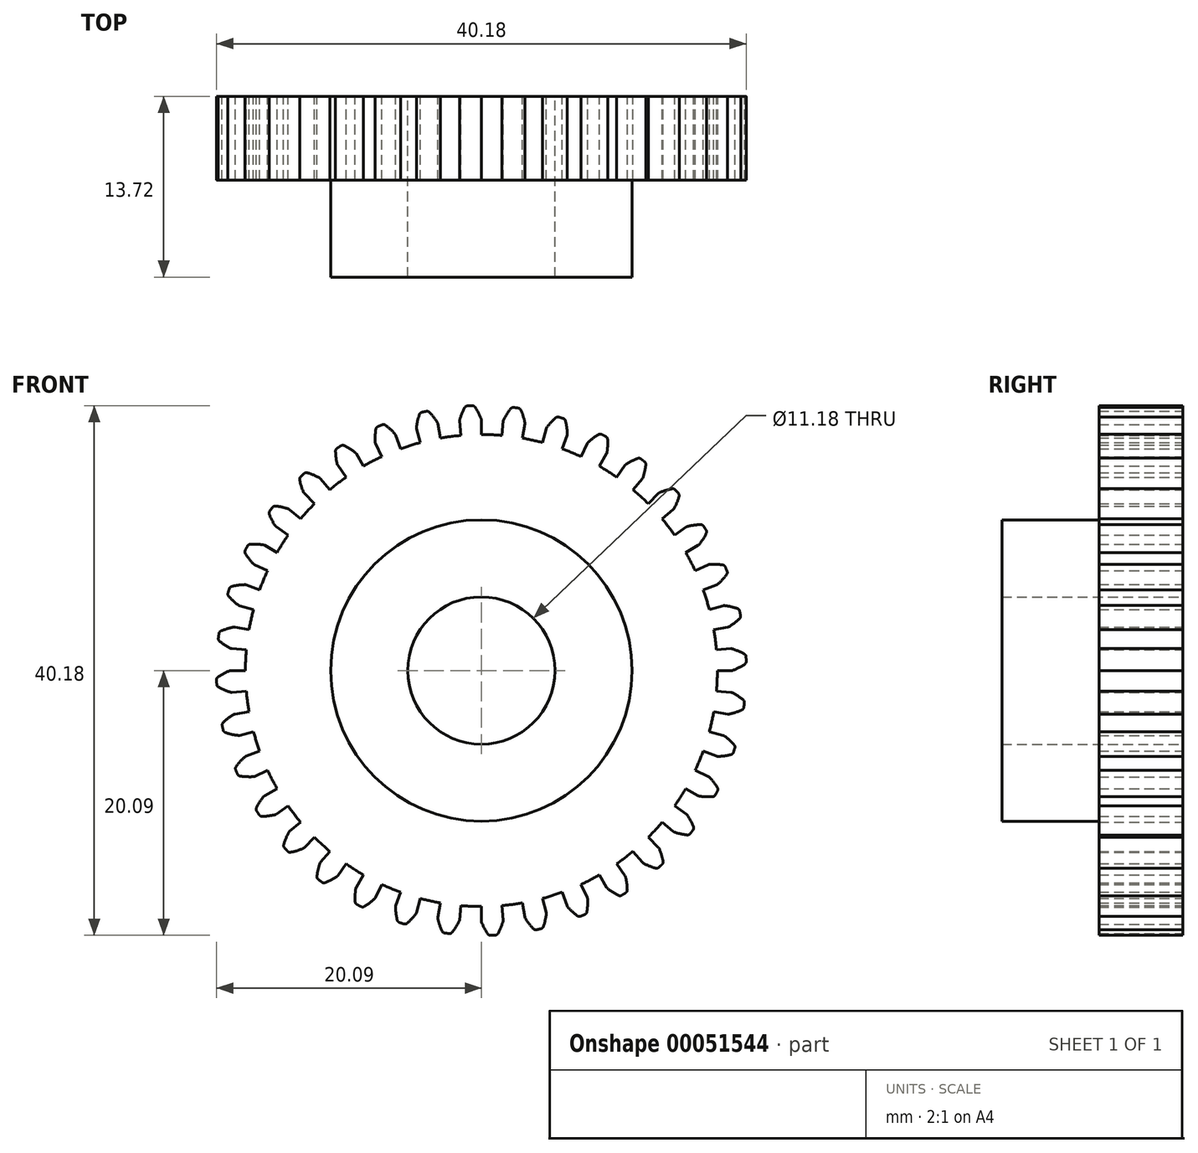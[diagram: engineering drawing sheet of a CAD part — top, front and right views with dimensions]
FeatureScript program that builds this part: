
annotation { "Feature Type Name" : "Feature", "Feature Type Description" : "" }
export const myFeature = defineFeature(function(context is Context, id is Id, definition is map)
    precondition{}
    {
        {
            var Q0;
            Q0=qCreatedBy(makeId("Front.planeOp"),FACE);
            var sketch = newSketch(context, id + "F0", { "sketchPlane" : qUnion([Q0])});
            skArc(sketch, "E0", {"start": v(-0.7, 20.1) * mm, "mid": v(-0.79, 20.09) * mm, "end": v(-0.88, 20.08) * mm});
            skCircle(sketch, "E1", {"center": v(0, 0) * mm, "radius": 17.9 * mm});
            skArc(sketch, "E2.trimOffspring", {"start": v(-0.02, 19.1) * mm, "mid": v(-0.23, 19.55) * mm, "end": v(-0.48, 19.98) * mm});
            skLineSegment(sketch, "E3", {"start": v(0, 19) * mm, "end": v(0, 17.9) * mm});
            skArc(sketch, "E4.MirrorCS", {"start": v(-1.05, 20.08) * mm, "mid": v(-0.97, 20.08) * mm, "end": v(-0.88, 20.08) * mm});
            skLineSegment(sketch, "E5.MirrorCS", {"start": v(-1.66, 18.93) * mm, "end": v(-1.56, 17.83) * mm});
            skArc(sketch, "E6.MirrorCS", {"start": v(-1.65, 19.02) * mm, "mid": v(-1.48, 19.5) * mm, "end": v(-1.26, 19.94) * mm});
            skPoint(sketch, "E7.visualSharp", {"position": v(-1.2, 20.07) * mm});
            skArc(sketch, "E7.filletArc", {"start": v(-1.05, 20.08) * mm, "mid": v(-1.18, 20.04) * mm, "end": v(-1.26, 19.94) * mm});
            skPoint(sketch, "E8.visualSharp", {"position": v(-0.56, 20.1) * mm});
            skArc(sketch, "E8.filletArc", {"start": v(-0.48, 19.98) * mm, "mid": v(-0.58, 20.06) * mm, "end": v(-0.7, 20.1) * mm});
            skPoint(sketch, "E9.visualSharp", {"position": v(-1.66, 18.98) * mm});
            skArc(sketch, "E9.filletArc", {"start": v(-1.65, 19.02) * mm, "mid": v(-1.66, 18.98) * mm, "end": v(-1.66, 18.93) * mm});
            skPoint(sketch, "E10.visualSharp", {"position": v(0, 19.05) * mm});
            skArc(sketch, "E10.filletArc", {"start": v(0, 19) * mm, "mid": v(0, 19.05) * mm, "end": v(-0.02, 19.1) * mm});
            skPoint(sketch, "E11.1.0", {"position": v(-3.3, 18.76) * mm});
            skPoint(sketch, "E11.1.1", {"position": v(-4.93, 18.4) * mm});
            skArc(sketch, "E11.1.2", {"start": v(-3.33, 18.8) * mm, "mid": v(-3.62, 19.21) * mm, "end": v(-3.94, 19.6) * mm});
            skLineSegment(sketch, "E11.1.3", {"start": v(-3.3, 18.71) * mm, "end": v(-3.1, 17.63) * mm});
            skLineSegment(sketch, "E11.1.4", {"start": v(-4.92, 18.36) * mm, "end": v(-4.63, 17.3) * mm});
            skArc(sketch, "E11.1.5", {"start": v(-4.93, 18.45) * mm, "mid": v(-4.84, 18.94) * mm, "end": v(-4.7, 19.42) * mm});
            skPoint(sketch, "E11.1.6", {"position": v(-4.04, 19.7) * mm});
            skPoint(sketch, "E11.1.7", {"position": v(-4.66, 19.56) * mm});
            skArc(sketch, "E11.1.8", {"start": v(-4.52, 19.59) * mm, "mid": v(-4.64, 19.53) * mm, "end": v(-4.7, 19.42) * mm});
            skArc(sketch, "E11.1.9", {"start": v(-4.18, 19.67) * mm, "mid": v(-4.27, 19.65) * mm, "end": v(-4.35, 19.63) * mm});
            skArc(sketch, "E11.1.10", {"start": v(-4.93, 18.45) * mm, "mid": v(-4.93, 18.4) * mm, "end": v(-4.92, 18.36) * mm});
            skArc(sketch, "E11.1.11", {"start": v(-3.3, 18.71) * mm, "mid": v(-3.31, 18.76) * mm, "end": v(-3.33, 18.8) * mm});
            skArc(sketch, "E11.1.12", {"start": v(-4.52, 19.59) * mm, "mid": v(-4.44, 19.6) * mm, "end": v(-4.35, 19.63) * mm});
            skArc(sketch, "E11.1.13", {"start": v(-3.94, 19.6) * mm, "mid": v(-4.05, 19.66) * mm, "end": v(-4.18, 19.67) * mm});
            skPoint(sketch, "E11.2.0", {"position": v(-6.52, 17.9) * mm});
            skPoint(sketch, "E11.2.1", {"position": v(-8.05, 17.27) * mm});
            skArc(sketch, "E11.2.2", {"start": v(-6.55, 17.94) * mm, "mid": v(-6.9, 18.3) * mm, "end": v(-7.28, 18.6) * mm});
            skLineSegment(sketch, "E11.2.3", {"start": v(-6.5, 17.86) * mm, "end": v(-6.12, 16.82) * mm});
            skLineSegment(sketch, "E11.2.4", {"start": v(-8.03, 17.22) * mm, "end": v(-7.57, 16.22) * mm});
            skArc(sketch, "E11.2.5", {"start": v(-8.05, 17.31) * mm, "mid": v(-8.06, 17.81) * mm, "end": v(-8, 18.3) * mm});
            skPoint(sketch, "E11.2.6", {"position": v(-7.4, 18.7) * mm});
            skPoint(sketch, "E11.2.7", {"position": v(-7.98, 18.45) * mm});
            skArc(sketch, "E11.2.8", {"start": v(-7.86, 18.5) * mm, "mid": v(-7.96, 18.43) * mm, "end": v(-8, 18.3) * mm});
            skArc(sketch, "E11.2.9", {"start": v(-7.53, 18.64) * mm, "mid": v(-7.61, 18.6) * mm, "end": v(-7.7, 18.57) * mm});
            skArc(sketch, "E11.2.10", {"start": v(-8.05, 17.31) * mm, "mid": v(-8.05, 17.27) * mm, "end": v(-8.03, 17.22) * mm});
            skArc(sketch, "E11.2.11", {"start": v(-6.5, 17.86) * mm, "mid": v(-6.52, 17.9) * mm, "end": v(-6.55, 17.94) * mm});
            skArc(sketch, "E11.2.12", {"start": v(-7.86, 18.5) * mm, "mid": v(-7.78, 18.54) * mm, "end": v(-7.7, 18.57) * mm});
            skArc(sketch, "E11.2.13", {"start": v(-7.28, 18.6) * mm, "mid": v(-7.4, 18.66) * mm, "end": v(-7.53, 18.64) * mm});
            skPoint(sketch, "E11.3.0", {"position": v(-9.52, 16.5) * mm});
            skPoint(sketch, "E11.3.1", {"position": v(-10.93, 15.6) * mm});
            skArc(sketch, "E11.3.2", {"start": v(-9.56, 16.53) * mm, "mid": v(-9.97, 16.82) * mm, "end": v(-10.4, 17.06) * mm});
            skLineSegment(sketch, "E11.3.3", {"start": v(-9.5, 16.46) * mm, "end": v(-8.95, 15.5) * mm});
            skLineSegment(sketch, "E11.3.4", {"start": v(-10.9, 15.57) * mm, "end": v(-10.27, 14.66) * mm});
            skArc(sketch, "E11.3.5", {"start": v(-10.94, 15.65) * mm, "mid": v(-11.03, 16.14) * mm, "end": v(-11.07, 16.64) * mm});
            skPoint(sketch, "E11.3.6", {"position": v(-10.53, 17.12) * mm});
            skPoint(sketch, "E11.3.7", {"position": v(-11.07, 16.78) * mm});
            skArc(sketch, "E11.3.8", {"start": v(-10.95, 16.86) * mm, "mid": v(-11.04, 16.77) * mm, "end": v(-11.07, 16.64) * mm});
            skArc(sketch, "E11.3.9", {"start": v(-10.65, 17.05) * mm, "mid": v(-10.73, 17) * mm, "end": v(-10.8, 16.96) * mm});
            skArc(sketch, "E11.3.10", {"start": v(-10.94, 15.65) * mm, "mid": v(-10.92, 15.6) * mm, "end": v(-10.9, 15.57) * mm});
            skArc(sketch, "E11.3.11", {"start": v(-9.5, 16.46) * mm, "mid": v(-9.53, 16.5) * mm, "end": v(-9.56, 16.53) * mm});
            skArc(sketch, "E11.3.12", {"start": v(-10.95, 16.86) * mm, "mid": v(-10.88, 16.9) * mm, "end": v(-10.8, 16.96) * mm});
            skArc(sketch, "E11.3.13", {"start": v(-10.4, 17.06) * mm, "mid": v(-10.53, 17.09) * mm, "end": v(-10.65, 17.05) * mm});
            skPoint(sketch, "E11.4.0", {"position": v(-12.25, 14.6) * mm});
            skPoint(sketch, "E11.4.1", {"position": v(-13.47, 13.47) * mm});
            skArc(sketch, "E11.4.2", {"start": v(-12.29, 14.62) * mm, "mid": v(-12.74, 14.83) * mm, "end": v(-13.2, 15) * mm});
            skLineSegment(sketch, "E11.4.3", {"start": v(-12.21, 14.56) * mm, "end": v(-11.5, 13.71) * mm});
            skLineSegment(sketch, "E11.4.4", {"start": v(-13.44, 13.44) * mm, "end": v(-12.66, 12.66) * mm});
            skArc(sketch, "E11.4.5", {"start": v(-13.49, 13.51) * mm, "mid": v(-13.66, 13.98) * mm, "end": v(-13.79, 14.47) * mm});
            skPoint(sketch, "E11.4.6", {"position": v(-13.35, 15.03) * mm});
            skPoint(sketch, "E11.4.7", {"position": v(-13.81, 14.6) * mm});
            skArc(sketch, "E11.4.8", {"start": v(-13.71, 14.7) * mm, "mid": v(-13.78, 14.6) * mm, "end": v(-13.79, 14.47) * mm});
            skArc(sketch, "E11.4.9", {"start": v(-13.45, 14.94) * mm, "mid": v(-13.52, 14.88) * mm, "end": v(-13.58, 14.82) * mm});
            skArc(sketch, "E11.4.10", {"start": v(-13.49, 13.51) * mm, "mid": v(-13.47, 13.47) * mm, "end": v(-13.44, 13.44) * mm});
            skArc(sketch, "E11.4.11", {"start": v(-12.21, 14.56) * mm, "mid": v(-12.25, 14.6) * mm, "end": v(-12.29, 14.62) * mm});
            skArc(sketch, "E11.4.12", {"start": v(-13.71, 14.7) * mm, "mid": v(-13.65, 14.76) * mm, "end": v(-13.58, 14.82) * mm});
            skArc(sketch, "E11.4.13", {"start": v(-13.2, 15) * mm, "mid": v(-13.34, 15) * mm, "end": v(-13.45, 14.94) * mm});
            skPoint(sketch, "E11.5.0", {"position": v(-14.6, 12.25) * mm});
            skPoint(sketch, "E11.5.1", {"position": v(-15.6, 10.93) * mm});
            skArc(sketch, "E11.5.2", {"start": v(-14.64, 12.26) * mm, "mid": v(-15.12, 12.4) * mm, "end": v(-15.61, 12.47) * mm});
            skLineSegment(sketch, "E11.5.3", {"start": v(-14.56, 12.21) * mm, "end": v(-13.71, 11.5) * mm});
            skLineSegment(sketch, "E11.5.4", {"start": v(-15.57, 10.9) * mm, "end": v(-14.66, 10.27) * mm});
            skArc(sketch, "E11.5.5", {"start": v(-15.63, 10.97) * mm, "mid": v(-15.88, 11.4) * mm, "end": v(-16.1, 11.85) * mm});
            skPoint(sketch, "E11.5.6", {"position": v(-15.76, 12.49) * mm});
            skPoint(sketch, "E11.5.7", {"position": v(-16.14, 11.99) * mm});
            skArc(sketch, "E11.5.8", {"start": v(-16.06, 12.1) * mm, "mid": v(-16.1, 11.98) * mm, "end": v(-16.1, 11.85) * mm});
            skArc(sketch, "E11.5.9", {"start": v(-15.84, 12.38) * mm, "mid": v(-15.9, 12.3) * mm, "end": v(-15.95, 12.24) * mm});
            skArc(sketch, "E11.5.10", {"start": v(-15.63, 10.97) * mm, "mid": v(-15.6, 10.93) * mm, "end": v(-15.57, 10.9) * mm});
            skArc(sketch, "E11.5.11", {"start": v(-14.56, 12.21) * mm, "mid": v(-14.6, 12.24) * mm, "end": v(-14.64, 12.26) * mm});
            skArc(sketch, "E11.5.12", {"start": v(-16.06, 12.1) * mm, "mid": v(-16, 12.17) * mm, "end": v(-15.95, 12.24) * mm});
            skArc(sketch, "E11.5.13", {"start": v(-15.61, 12.47) * mm, "mid": v(-15.74, 12.46) * mm, "end": v(-15.84, 12.38) * mm});
            skPoint(sketch, "E11.6.0", {"position": v(-16.5, 9.52) * mm});
            skPoint(sketch, "E11.6.1", {"position": v(-17.27, 8.05) * mm});
            skArc(sketch, "E11.6.2", {"start": v(-16.55, 9.53) * mm, "mid": v(-17.04, 9.58) * mm, "end": v(-17.54, 9.57) * mm});
            skLineSegment(sketch, "E11.6.3", {"start": v(-16.46, 9.5) * mm, "end": v(-15.5, 8.95) * mm});
            skLineSegment(sketch, "E11.6.4", {"start": v(-17.22, 8.03) * mm, "end": v(-16.22, 7.57) * mm});
            skArc(sketch, "E11.6.5", {"start": v(-17.3, 8.09) * mm, "mid": v(-17.62, 8.47) * mm, "end": v(-17.9, 8.88) * mm});
            skPoint(sketch, "E11.6.6", {"position": v(-17.68, 9.56) * mm});
            skPoint(sketch, "E11.6.7", {"position": v(-17.98, 9) * mm});
            skArc(sketch, "E11.6.8", {"start": v(-17.91, 9.13) * mm, "mid": v(-17.94, 9) * mm, "end": v(-17.9, 8.88) * mm});
            skArc(sketch, "E11.6.9", {"start": v(-17.75, 9.44) * mm, "mid": v(-17.8, 9.36) * mm, "end": v(-17.83, 9.28) * mm});
            skArc(sketch, "E11.6.10", {"start": v(-17.3, 8.09) * mm, "mid": v(-17.26, 8.05) * mm, "end": v(-17.22, 8.03) * mm});
            skArc(sketch, "E11.6.11", {"start": v(-16.46, 9.5) * mm, "mid": v(-16.5, 9.52) * mm, "end": v(-16.55, 9.53) * mm});
            skArc(sketch, "E11.6.12", {"start": v(-17.91, 9.13) * mm, "mid": v(-17.87, 9.2) * mm, "end": v(-17.83, 9.28) * mm});
            skArc(sketch, "E11.6.13", {"start": v(-17.54, 9.57) * mm, "mid": v(-17.66, 9.53) * mm, "end": v(-17.75, 9.44) * mm});
            skPoint(sketch, "E11.7.0", {"position": v(-17.9, 6.52) * mm});
            skPoint(sketch, "E11.7.1", {"position": v(-18.4, 4.93) * mm});
            skArc(sketch, "E11.7.2", {"start": v(-17.95, 6.51) * mm, "mid": v(-18.45, 6.47) * mm, "end": v(-18.94, 6.38) * mm});
            skLineSegment(sketch, "E11.7.3", {"start": v(-17.86, 6.5) * mm, "end": v(-16.82, 6.12) * mm});
            skLineSegment(sketch, "E11.7.4", {"start": v(-18.36, 4.92) * mm, "end": v(-17.3, 4.63) * mm});
            skArc(sketch, "E11.7.5", {"start": v(-18.44, 4.96) * mm, "mid": v(-18.82, 5.28) * mm, "end": v(-19.17, 5.63) * mm});
            skPoint(sketch, "E11.7.6", {"position": v(-19.08, 6.35) * mm});
            skPoint(sketch, "E11.7.7", {"position": v(-19.27, 5.74) * mm});
            skArc(sketch, "E11.7.8", {"start": v(-19.23, 5.88) * mm, "mid": v(-19.23, 5.75) * mm, "end": v(-19.17, 5.63) * mm});
            skArc(sketch, "E11.7.9", {"start": v(-19.12, 6.21) * mm, "mid": v(-19.15, 6.13) * mm, "end": v(-19.17, 6.05) * mm});
            skArc(sketch, "E11.7.10", {"start": v(-18.44, 4.96) * mm, "mid": v(-18.4, 4.93) * mm, "end": v(-18.36, 4.92) * mm});
            skArc(sketch, "E11.7.11", {"start": v(-17.86, 6.5) * mm, "mid": v(-17.9, 6.51) * mm, "end": v(-17.95, 6.51) * mm});
            skArc(sketch, "E11.7.12", {"start": v(-19.23, 5.88) * mm, "mid": v(-19.2, 5.96) * mm, "end": v(-19.17, 6.05) * mm});
            skArc(sketch, "E11.7.13", {"start": v(-18.94, 6.38) * mm, "mid": v(-19.05, 6.32) * mm, "end": v(-19.12, 6.21) * mm});
            skPoint(sketch, "E11.8.0", {"position": v(-18.76, 3.3) * mm});
            skPoint(sketch, "E11.8.1", {"position": v(-18.98, 1.66) * mm});
            skArc(sketch, "E11.8.2", {"start": v(-18.8, 3.3) * mm, "mid": v(-19.3, 3.17) * mm, "end": v(-19.76, 3) * mm});
            skLineSegment(sketch, "E11.8.3", {"start": v(-18.71, 3.3) * mm, "end": v(-17.63, 3.1) * mm});
            skLineSegment(sketch, "E11.8.4", {"start": v(-18.93, 1.66) * mm, "end": v(-17.83, 1.56) * mm});
            skArc(sketch, "E11.8.5", {"start": v(-19.02, 1.68) * mm, "mid": v(-19.46, 1.93) * mm, "end": v(-19.86, 2.22) * mm});
            skPoint(sketch, "E11.8.6", {"position": v(-19.89, 2.94) * mm});
            skPoint(sketch, "E11.8.7", {"position": v(-19.97, 2.31) * mm});
            skArc(sketch, "E11.8.8", {"start": v(-19.95, 2.45) * mm, "mid": v(-19.94, 2.32) * mm, "end": v(-19.86, 2.22) * mm});
            skArc(sketch, "E11.8.9", {"start": v(-19.9, 2.8) * mm, "mid": v(-19.92, 2.71) * mm, "end": v(-19.93, 2.62) * mm});
            skArc(sketch, "E11.8.10", {"start": v(-19.02, 1.68) * mm, "mid": v(-18.98, 1.66) * mm, "end": v(-18.93, 1.66) * mm});
            skArc(sketch, "E11.8.11", {"start": v(-18.71, 3.3) * mm, "mid": v(-18.76, 3.3) * mm, "end": v(-18.8, 3.3) * mm});
            skArc(sketch, "E11.8.12", {"start": v(-19.95, 2.45) * mm, "mid": v(-19.94, 2.54) * mm, "end": v(-19.93, 2.62) * mm});
            skArc(sketch, "E11.8.13", {"start": v(-19.76, 3) * mm, "mid": v(-19.86, 2.92) * mm, "end": v(-19.9, 2.8) * mm});
            skPoint(sketch, "E11.9.0", {"position": v(-19.05, 0) * mm});
            skPoint(sketch, "E11.9.1", {"position": v(-18.98, -1.66) * mm});
            skArc(sketch, "E11.9.2", {"start": v(-19.1, -0.02) * mm, "mid": v(-19.55, -0.23) * mm, "end": v(-19.98, -0.48) * mm});
            skLineSegment(sketch, "E11.9.3", {"start": v(-19, 0) * mm, "end": v(-17.9, 0) * mm});
            skLineSegment(sketch, "E11.9.4", {"start": v(-18.93, -1.66) * mm, "end": v(-17.83, -1.56) * mm});
            skArc(sketch, "E11.9.5", {"start": v(-19.02, -1.65) * mm, "mid": v(-19.5, -1.48) * mm, "end": v(-19.94, -1.26) * mm});
            skPoint(sketch, "E11.9.6", {"position": v(-20.1, -0.56) * mm});
            skPoint(sketch, "E11.9.7", {"position": v(-20.07, -1.2) * mm});
            skArc(sketch, "E11.9.8", {"start": v(-20.08, -1.05) * mm, "mid": v(-20.04, -1.18) * mm, "end": v(-19.94, -1.26) * mm});
            skArc(sketch, "E11.9.9", {"start": v(-20.1, -0.7) * mm, "mid": v(-20.09, -0.79) * mm, "end": v(-20.08, -0.88) * mm});
            skArc(sketch, "E11.9.10", {"start": v(-19.02, -1.65) * mm, "mid": v(-18.98, -1.66) * mm, "end": v(-18.93, -1.66) * mm});
            skArc(sketch, "E11.9.11", {"start": v(-19, 0) * mm, "mid": v(-19.05, 0) * mm, "end": v(-19.1, -0.02) * mm});
            skArc(sketch, "E11.9.12", {"start": v(-20.08, -1.05) * mm, "mid": v(-20.08, -0.97) * mm, "end": v(-20.08, -0.88) * mm});
            skArc(sketch, "E11.9.13", {"start": v(-19.98, -0.48) * mm, "mid": v(-20.06, -0.58) * mm, "end": v(-20.1, -0.7) * mm});
            skPoint(sketch, "E11.10.0", {"position": v(-18.76, -3.3) * mm});
            skPoint(sketch, "E11.10.1", {"position": v(-18.4, -4.93) * mm});
            skArc(sketch, "E11.10.2", {"start": v(-18.8, -3.33) * mm, "mid": v(-19.21, -3.62) * mm, "end": v(-19.6, -3.94) * mm});
            skLineSegment(sketch, "E11.10.3", {"start": v(-18.71, -3.3) * mm, "end": v(-17.63, -3.1) * mm});
            skLineSegment(sketch, "E11.10.4", {"start": v(-18.36, -4.92) * mm, "end": v(-17.3, -4.63) * mm});
            skArc(sketch, "E11.10.5", {"start": v(-18.45, -4.93) * mm, "mid": v(-18.94, -4.84) * mm, "end": v(-19.42, -4.7) * mm});
            skPoint(sketch, "E11.10.6", {"position": v(-19.7, -4.04) * mm});
            skPoint(sketch, "E11.10.7", {"position": v(-19.56, -4.66) * mm});
            skArc(sketch, "E11.10.8", {"start": v(-19.59, -4.52) * mm, "mid": v(-19.53, -4.64) * mm, "end": v(-19.42, -4.7) * mm});
            skArc(sketch, "E11.10.9", {"start": v(-19.67, -4.18) * mm, "mid": v(-19.65, -4.27) * mm, "end": v(-19.63, -4.35) * mm});
            skArc(sketch, "E11.10.10", {"start": v(-18.45, -4.93) * mm, "mid": v(-18.4, -4.93) * mm, "end": v(-18.36, -4.92) * mm});
            skArc(sketch, "E11.10.11", {"start": v(-18.71, -3.3) * mm, "mid": v(-18.76, -3.31) * mm, "end": v(-18.8, -3.33) * mm});
            skArc(sketch, "E11.10.12", {"start": v(-19.59, -4.52) * mm, "mid": v(-19.6, -4.44) * mm, "end": v(-19.63, -4.35) * mm});
            skArc(sketch, "E11.10.13", {"start": v(-19.6, -3.94) * mm, "mid": v(-19.66, -4.05) * mm, "end": v(-19.67, -4.18) * mm});
            skPoint(sketch, "E11.11.0", {"position": v(-17.9, -6.52) * mm});
            skPoint(sketch, "E11.11.1", {"position": v(-17.27, -8.05) * mm});
            skArc(sketch, "E11.11.2", {"start": v(-17.94, -6.55) * mm, "mid": v(-18.3, -6.9) * mm, "end": v(-18.6, -7.28) * mm});
            skLineSegment(sketch, "E11.11.3", {"start": v(-17.86, -6.5) * mm, "end": v(-16.82, -6.12) * mm});
            skLineSegment(sketch, "E11.11.4", {"start": v(-17.22, -8.03) * mm, "end": v(-16.22, -7.57) * mm});
            skArc(sketch, "E11.11.5", {"start": v(-17.31, -8.05) * mm, "mid": v(-17.81, -8.06) * mm, "end": v(-18.3, -8) * mm});
            skPoint(sketch, "E11.11.6", {"position": v(-18.7, -7.4) * mm});
            skPoint(sketch, "E11.11.7", {"position": v(-18.45, -7.98) * mm});
            skArc(sketch, "E11.11.8", {"start": v(-18.5, -7.86) * mm, "mid": v(-18.43, -7.96) * mm, "end": v(-18.3, -8) * mm});
            skArc(sketch, "E11.11.9", {"start": v(-18.64, -7.53) * mm, "mid": v(-18.6, -7.61) * mm, "end": v(-18.57, -7.7) * mm});
            skArc(sketch, "E11.11.10", {"start": v(-17.31, -8.05) * mm, "mid": v(-17.27, -8.05) * mm, "end": v(-17.22, -8.03) * mm});
            skArc(sketch, "E11.11.11", {"start": v(-17.86, -6.5) * mm, "mid": v(-17.9, -6.52) * mm, "end": v(-17.94, -6.55) * mm});
            skArc(sketch, "E11.11.12", {"start": v(-18.5, -7.86) * mm, "mid": v(-18.54, -7.78) * mm, "end": v(-18.57, -7.7) * mm});
            skArc(sketch, "E11.11.13", {"start": v(-18.6, -7.28) * mm, "mid": v(-18.66, -7.4) * mm, "end": v(-18.64, -7.53) * mm});
            skPoint(sketch, "E11.12.0", {"position": v(-16.5, -9.52) * mm});
            skPoint(sketch, "E11.12.1", {"position": v(-15.6, -10.93) * mm});
            skArc(sketch, "E11.12.2", {"start": v(-16.53, -9.56) * mm, "mid": v(-16.82, -9.97) * mm, "end": v(-17.06, -10.4) * mm});
            skLineSegment(sketch, "E11.12.3", {"start": v(-16.46, -9.5) * mm, "end": v(-15.5, -8.95) * mm});
            skLineSegment(sketch, "E11.12.4", {"start": v(-15.57, -10.9) * mm, "end": v(-14.66, -10.27) * mm});
            skArc(sketch, "E11.12.5", {"start": v(-15.65, -10.94) * mm, "mid": v(-16.14, -11.03) * mm, "end": v(-16.64, -11.07) * mm});
            skPoint(sketch, "E11.12.6", {"position": v(-17.12, -10.53) * mm});
            skPoint(sketch, "E11.12.7", {"position": v(-16.78, -11.07) * mm});
            skArc(sketch, "E11.12.8", {"start": v(-16.86, -10.95) * mm, "mid": v(-16.77, -11.04) * mm, "end": v(-16.64, -11.07) * mm});
            skArc(sketch, "E11.12.9", {"start": v(-17.05, -10.65) * mm, "mid": v(-17, -10.73) * mm, "end": v(-16.96, -10.8) * mm});
            skArc(sketch, "E11.12.10", {"start": v(-15.65, -10.94) * mm, "mid": v(-15.6, -10.92) * mm, "end": v(-15.57, -10.9) * mm});
            skArc(sketch, "E11.12.11", {"start": v(-16.46, -9.5) * mm, "mid": v(-16.5, -9.53) * mm, "end": v(-16.53, -9.56) * mm});
            skArc(sketch, "E11.12.12", {"start": v(-16.86, -10.95) * mm, "mid": v(-16.9, -10.88) * mm, "end": v(-16.96, -10.8) * mm});
            skArc(sketch, "E11.12.13", {"start": v(-17.06, -10.4) * mm, "mid": v(-17.09, -10.53) * mm, "end": v(-17.05, -10.65) * mm});
            skPoint(sketch, "E11.13.0", {"position": v(-14.6, -12.25) * mm});
            skPoint(sketch, "E11.13.1", {"position": v(-13.47, -13.47) * mm});
            skArc(sketch, "E11.13.2", {"start": v(-14.62, -12.29) * mm, "mid": v(-14.83, -12.74) * mm, "end": v(-15, -13.2) * mm});
            skLineSegment(sketch, "E11.13.3", {"start": v(-14.56, -12.21) * mm, "end": v(-13.71, -11.5) * mm});
            skLineSegment(sketch, "E11.13.4", {"start": v(-13.44, -13.44) * mm, "end": v(-12.66, -12.66) * mm});
            skArc(sketch, "E11.13.5", {"start": v(-13.51, -13.49) * mm, "mid": v(-13.98, -13.66) * mm, "end": v(-14.47, -13.79) * mm});
            skPoint(sketch, "E11.13.6", {"position": v(-15.03, -13.35) * mm});
            skPoint(sketch, "E11.13.7", {"position": v(-14.6, -13.81) * mm});
            skArc(sketch, "E11.13.8", {"start": v(-14.7, -13.71) * mm, "mid": v(-14.6, -13.78) * mm, "end": v(-14.47, -13.79) * mm});
            skArc(sketch, "E11.13.9", {"start": v(-14.94, -13.45) * mm, "mid": v(-14.88, -13.52) * mm, "end": v(-14.82, -13.58) * mm});
            skArc(sketch, "E11.13.10", {"start": v(-13.51, -13.49) * mm, "mid": v(-13.47, -13.47) * mm, "end": v(-13.44, -13.44) * mm});
            skArc(sketch, "E11.13.11", {"start": v(-14.56, -12.21) * mm, "mid": v(-14.6, -12.25) * mm, "end": v(-14.62, -12.29) * mm});
            skArc(sketch, "E11.13.12", {"start": v(-14.7, -13.71) * mm, "mid": v(-14.76, -13.65) * mm, "end": v(-14.82, -13.58) * mm});
            skArc(sketch, "E11.13.13", {"start": v(-15, -13.2) * mm, "mid": v(-15, -13.34) * mm, "end": v(-14.94, -13.45) * mm});
            skPoint(sketch, "E11.14.0", {"position": v(-12.25, -14.6) * mm});
            skPoint(sketch, "E11.14.1", {"position": v(-10.93, -15.6) * mm});
            skArc(sketch, "E11.14.2", {"start": v(-12.26, -14.64) * mm, "mid": v(-12.4, -15.12) * mm, "end": v(-12.47, -15.61) * mm});
            skLineSegment(sketch, "E11.14.3", {"start": v(-12.21, -14.56) * mm, "end": v(-11.5, -13.71) * mm});
            skLineSegment(sketch, "E11.14.4", {"start": v(-10.9, -15.57) * mm, "end": v(-10.27, -14.66) * mm});
            skArc(sketch, "E11.14.5", {"start": v(-10.97, -15.63) * mm, "mid": v(-11.4, -15.88) * mm, "end": v(-11.85, -16.1) * mm});
            skPoint(sketch, "E11.14.6", {"position": v(-12.49, -15.76) * mm});
            skPoint(sketch, "E11.14.7", {"position": v(-11.99, -16.14) * mm});
            skArc(sketch, "E11.14.8", {"start": v(-12.1, -16.06) * mm, "mid": v(-11.98, -16.1) * mm, "end": v(-11.85, -16.1) * mm});
            skArc(sketch, "E11.14.9", {"start": v(-12.38, -15.84) * mm, "mid": v(-12.3, -15.9) * mm, "end": v(-12.24, -15.95) * mm});
            skArc(sketch, "E11.14.10", {"start": v(-10.97, -15.63) * mm, "mid": v(-10.93, -15.6) * mm, "end": v(-10.9, -15.57) * mm});
            skArc(sketch, "E11.14.11", {"start": v(-12.21, -14.56) * mm, "mid": v(-12.24, -14.6) * mm, "end": v(-12.26, -14.64) * mm});
            skArc(sketch, "E11.14.12", {"start": v(-12.1, -16.06) * mm, "mid": v(-12.17, -16) * mm, "end": v(-12.24, -15.95) * mm});
            skArc(sketch, "E11.14.13", {"start": v(-12.47, -15.61) * mm, "mid": v(-12.46, -15.74) * mm, "end": v(-12.38, -15.84) * mm});
            skPoint(sketch, "E11.15.0", {"position": v(-9.52, -16.5) * mm});
            skPoint(sketch, "E11.15.1", {"position": v(-8.05, -17.27) * mm});
            skArc(sketch, "E11.15.2", {"start": v(-9.53, -16.55) * mm, "mid": v(-9.58, -17.04) * mm, "end": v(-9.57, -17.54) * mm});
            skLineSegment(sketch, "E11.15.3", {"start": v(-9.5, -16.46) * mm, "end": v(-8.95, -15.5) * mm});
            skLineSegment(sketch, "E11.15.4", {"start": v(-8.03, -17.22) * mm, "end": v(-7.57, -16.22) * mm});
            skArc(sketch, "E11.15.5", {"start": v(-8.09, -17.3) * mm, "mid": v(-8.47, -17.62) * mm, "end": v(-8.88, -17.9) * mm});
            skPoint(sketch, "E11.15.6", {"position": v(-9.56, -17.68) * mm});
            skPoint(sketch, "E11.15.7", {"position": v(-9, -17.98) * mm});
            skArc(sketch, "E11.15.8", {"start": v(-9.13, -17.91) * mm, "mid": v(-9, -17.94) * mm, "end": v(-8.88, -17.9) * mm});
            skArc(sketch, "E11.15.9", {"start": v(-9.44, -17.75) * mm, "mid": v(-9.36, -17.8) * mm, "end": v(-9.28, -17.83) * mm});
            skArc(sketch, "E11.15.10", {"start": v(-8.09, -17.3) * mm, "mid": v(-8.05, -17.26) * mm, "end": v(-8.03, -17.22) * mm});
            skArc(sketch, "E11.15.11", {"start": v(-9.5, -16.46) * mm, "mid": v(-9.52, -16.5) * mm, "end": v(-9.53, -16.55) * mm});
            skArc(sketch, "E11.15.12", {"start": v(-9.13, -17.91) * mm, "mid": v(-9.2, -17.87) * mm, "end": v(-9.28, -17.83) * mm});
            skArc(sketch, "E11.15.13", {"start": v(-9.57, -17.54) * mm, "mid": v(-9.53, -17.66) * mm, "end": v(-9.44, -17.75) * mm});
            skPoint(sketch, "E11.16.0", {"position": v(-6.52, -17.9) * mm});
            skPoint(sketch, "E11.16.1", {"position": v(-4.93, -18.4) * mm});
            skArc(sketch, "E11.16.2", {"start": v(-6.51, -17.95) * mm, "mid": v(-6.47, -18.45) * mm, "end": v(-6.38, -18.94) * mm});
            skLineSegment(sketch, "E11.16.3", {"start": v(-6.5, -17.86) * mm, "end": v(-6.12, -16.82) * mm});
            skLineSegment(sketch, "E11.16.4", {"start": v(-4.92, -18.36) * mm, "end": v(-4.63, -17.3) * mm});
            skArc(sketch, "E11.16.5", {"start": v(-4.96, -18.44) * mm, "mid": v(-5.28, -18.82) * mm, "end": v(-5.63, -19.17) * mm});
            skPoint(sketch, "E11.16.6", {"position": v(-6.35, -19.08) * mm});
            skPoint(sketch, "E11.16.7", {"position": v(-5.74, -19.27) * mm});
            skArc(sketch, "E11.16.8", {"start": v(-5.88, -19.23) * mm, "mid": v(-5.75, -19.23) * mm, "end": v(-5.63, -19.17) * mm});
            skArc(sketch, "E11.16.9", {"start": v(-6.21, -19.12) * mm, "mid": v(-6.13, -19.15) * mm, "end": v(-6.05, -19.17) * mm});
            skArc(sketch, "E11.16.10", {"start": v(-4.96, -18.44) * mm, "mid": v(-4.93, -18.4) * mm, "end": v(-4.92, -18.36) * mm});
            skArc(sketch, "E11.16.11", {"start": v(-6.5, -17.86) * mm, "mid": v(-6.51, -17.9) * mm, "end": v(-6.51, -17.95) * mm});
            skArc(sketch, "E11.16.12", {"start": v(-5.88, -19.23) * mm, "mid": v(-5.96, -19.2) * mm, "end": v(-6.05, -19.17) * mm});
            skArc(sketch, "E11.16.13", {"start": v(-6.38, -18.94) * mm, "mid": v(-6.32, -19.05) * mm, "end": v(-6.21, -19.12) * mm});
            skPoint(sketch, "E11.17.0", {"position": v(-3.3, -18.76) * mm});
            skPoint(sketch, "E11.17.1", {"position": v(-1.66, -18.98) * mm});
            skArc(sketch, "E11.17.2", {"start": v(-3.3, -18.8) * mm, "mid": v(-3.17, -19.3) * mm, "end": v(-3, -19.76) * mm});
            skLineSegment(sketch, "E11.17.3", {"start": v(-3.3, -18.71) * mm, "end": v(-3.1, -17.63) * mm});
            skLineSegment(sketch, "E11.17.4", {"start": v(-1.66, -18.93) * mm, "end": v(-1.56, -17.83) * mm});
            skArc(sketch, "E11.17.5", {"start": v(-1.68, -19.02) * mm, "mid": v(-1.93, -19.46) * mm, "end": v(-2.22, -19.86) * mm});
            skPoint(sketch, "E11.17.6", {"position": v(-2.94, -19.89) * mm});
            skPoint(sketch, "E11.17.7", {"position": v(-2.31, -19.97) * mm});
            skArc(sketch, "E11.17.8", {"start": v(-2.45, -19.95) * mm, "mid": v(-2.32, -19.94) * mm, "end": v(-2.22, -19.86) * mm});
            skArc(sketch, "E11.17.9", {"start": v(-2.8, -19.9) * mm, "mid": v(-2.71, -19.92) * mm, "end": v(-2.62, -19.93) * mm});
            skArc(sketch, "E11.17.10", {"start": v(-1.68, -19.02) * mm, "mid": v(-1.66, -18.98) * mm, "end": v(-1.66, -18.93) * mm});
            skArc(sketch, "E11.17.11", {"start": v(-3.3, -18.71) * mm, "mid": v(-3.3, -18.76) * mm, "end": v(-3.3, -18.8) * mm});
            skArc(sketch, "E11.17.12", {"start": v(-2.45, -19.95) * mm, "mid": v(-2.54, -19.94) * mm, "end": v(-2.62, -19.93) * mm});
            skArc(sketch, "E11.17.13", {"start": v(-3, -19.76) * mm, "mid": v(-2.92, -19.86) * mm, "end": v(-2.8, -19.9) * mm});
            skPoint(sketch, "E11.18.0", {"position": v(0, -19.05) * mm});
            skPoint(sketch, "E11.18.1", {"position": v(1.66, -18.98) * mm});
            skArc(sketch, "E11.18.2", {"start": v(0.02, -19.1) * mm, "mid": v(0.23, -19.55) * mm, "end": v(0.48, -19.98) * mm});
            skLineSegment(sketch, "E11.18.3", {"start": v(0, -19) * mm, "end": v(0, -17.9) * mm});
            skLineSegment(sketch, "E11.18.4", {"start": v(1.66, -18.93) * mm, "end": v(1.56, -17.83) * mm});
            skArc(sketch, "E11.18.5", {"start": v(1.65, -19.02) * mm, "mid": v(1.48, -19.5) * mm, "end": v(1.26, -19.94) * mm});
            skPoint(sketch, "E11.18.6", {"position": v(0.56, -20.1) * mm});
            skPoint(sketch, "E11.18.7", {"position": v(1.2, -20.07) * mm});
            skArc(sketch, "E11.18.8", {"start": v(1.05, -20.08) * mm, "mid": v(1.18, -20.04) * mm, "end": v(1.26, -19.94) * mm});
            skArc(sketch, "E11.18.9", {"start": v(0.7, -20.1) * mm, "mid": v(0.79, -20.09) * mm, "end": v(0.88, -20.08) * mm});
            skArc(sketch, "E11.18.10", {"start": v(1.65, -19.02) * mm, "mid": v(1.66, -18.98) * mm, "end": v(1.66, -18.93) * mm});
            skArc(sketch, "E11.18.11", {"start": v(0, -19) * mm, "mid": v(0, -19.05) * mm, "end": v(0.02, -19.1) * mm});
            skArc(sketch, "E11.18.12", {"start": v(1.05, -20.08) * mm, "mid": v(0.97, -20.08) * mm, "end": v(0.88, -20.08) * mm});
            skArc(sketch, "E11.18.13", {"start": v(0.48, -19.98) * mm, "mid": v(0.58, -20.06) * mm, "end": v(0.7, -20.1) * mm});
            skPoint(sketch, "E11.19.0", {"position": v(3.3, -18.76) * mm});
            skPoint(sketch, "E11.19.1", {"position": v(4.93, -18.4) * mm});
            skArc(sketch, "E11.19.2", {"start": v(3.33, -18.8) * mm, "mid": v(3.62, -19.21) * mm, "end": v(3.94, -19.6) * mm});
            skLineSegment(sketch, "E11.19.3", {"start": v(3.3, -18.71) * mm, "end": v(3.1, -17.63) * mm});
            skLineSegment(sketch, "E11.19.4", {"start": v(4.92, -18.36) * mm, "end": v(4.63, -17.3) * mm});
            skArc(sketch, "E11.19.5", {"start": v(4.93, -18.45) * mm, "mid": v(4.84, -18.94) * mm, "end": v(4.7, -19.42) * mm});
            skPoint(sketch, "E11.19.6", {"position": v(4.04, -19.7) * mm});
            skPoint(sketch, "E11.19.7", {"position": v(4.66, -19.56) * mm});
            skArc(sketch, "E11.19.8", {"start": v(4.52, -19.59) * mm, "mid": v(4.64, -19.53) * mm, "end": v(4.7, -19.42) * mm});
            skArc(sketch, "E11.19.9", {"start": v(4.18, -19.67) * mm, "mid": v(4.27, -19.65) * mm, "end": v(4.35, -19.63) * mm});
            skArc(sketch, "E11.19.10", {"start": v(4.93, -18.45) * mm, "mid": v(4.93, -18.4) * mm, "end": v(4.92, -18.36) * mm});
            skArc(sketch, "E11.19.11", {"start": v(3.3, -18.71) * mm, "mid": v(3.31, -18.76) * mm, "end": v(3.33, -18.8) * mm});
            skArc(sketch, "E11.19.12", {"start": v(4.52, -19.59) * mm, "mid": v(4.44, -19.6) * mm, "end": v(4.35, -19.63) * mm});
            skArc(sketch, "E11.19.13", {"start": v(3.94, -19.6) * mm, "mid": v(4.05, -19.66) * mm, "end": v(4.18, -19.67) * mm});
            skPoint(sketch, "E11.20.0", {"position": v(6.52, -17.9) * mm});
            skPoint(sketch, "E11.20.1", {"position": v(8.05, -17.27) * mm});
            skArc(sketch, "E11.20.2", {"start": v(6.55, -17.94) * mm, "mid": v(6.9, -18.3) * mm, "end": v(7.28, -18.6) * mm});
            skLineSegment(sketch, "E11.20.3", {"start": v(6.5, -17.86) * mm, "end": v(6.12, -16.82) * mm});
            skLineSegment(sketch, "E11.20.4", {"start": v(8.03, -17.22) * mm, "end": v(7.57, -16.22) * mm});
            skArc(sketch, "E11.20.5", {"start": v(8.05, -17.31) * mm, "mid": v(8.06, -17.81) * mm, "end": v(8, -18.3) * mm});
            skPoint(sketch, "E11.20.6", {"position": v(7.4, -18.7) * mm});
            skPoint(sketch, "E11.20.7", {"position": v(7.98, -18.45) * mm});
            skArc(sketch, "E11.20.8", {"start": v(7.86, -18.5) * mm, "mid": v(7.96, -18.43) * mm, "end": v(8, -18.3) * mm});
            skArc(sketch, "E11.20.9", {"start": v(7.53, -18.64) * mm, "mid": v(7.61, -18.6) * mm, "end": v(7.7, -18.57) * mm});
            skArc(sketch, "E11.20.10", {"start": v(8.05, -17.31) * mm, "mid": v(8.05, -17.27) * mm, "end": v(8.03, -17.22) * mm});
            skArc(sketch, "E11.20.11", {"start": v(6.5, -17.86) * mm, "mid": v(6.52, -17.9) * mm, "end": v(6.55, -17.94) * mm});
            skArc(sketch, "E11.20.12", {"start": v(7.86, -18.5) * mm, "mid": v(7.78, -18.54) * mm, "end": v(7.7, -18.57) * mm});
            skArc(sketch, "E11.20.13", {"start": v(7.28, -18.6) * mm, "mid": v(7.4, -18.66) * mm, "end": v(7.53, -18.64) * mm});
            skPoint(sketch, "E11.21.0", {"position": v(9.52, -16.5) * mm});
            skPoint(sketch, "E11.21.1", {"position": v(10.93, -15.6) * mm});
            skArc(sketch, "E11.21.2", {"start": v(9.56, -16.53) * mm, "mid": v(9.97, -16.82) * mm, "end": v(10.4, -17.06) * mm});
            skLineSegment(sketch, "E11.21.3", {"start": v(9.5, -16.46) * mm, "end": v(8.95, -15.5) * mm});
            skLineSegment(sketch, "E11.21.4", {"start": v(10.9, -15.57) * mm, "end": v(10.27, -14.66) * mm});
            skArc(sketch, "E11.21.5", {"start": v(10.94, -15.65) * mm, "mid": v(11.03, -16.14) * mm, "end": v(11.07, -16.64) * mm});
            skPoint(sketch, "E11.21.6", {"position": v(10.53, -17.12) * mm});
            skPoint(sketch, "E11.21.7", {"position": v(11.07, -16.78) * mm});
            skArc(sketch, "E11.21.8", {"start": v(10.95, -16.86) * mm, "mid": v(11.04, -16.77) * mm, "end": v(11.07, -16.64) * mm});
            skArc(sketch, "E11.21.9", {"start": v(10.65, -17.05) * mm, "mid": v(10.73, -17) * mm, "end": v(10.8, -16.96) * mm});
            skArc(sketch, "E11.21.10", {"start": v(10.94, -15.65) * mm, "mid": v(10.92, -15.6) * mm, "end": v(10.9, -15.57) * mm});
            skArc(sketch, "E11.21.11", {"start": v(9.5, -16.46) * mm, "mid": v(9.53, -16.5) * mm, "end": v(9.56, -16.53) * mm});
            skArc(sketch, "E11.21.12", {"start": v(10.95, -16.86) * mm, "mid": v(10.88, -16.9) * mm, "end": v(10.8, -16.96) * mm});
            skArc(sketch, "E11.21.13", {"start": v(10.4, -17.06) * mm, "mid": v(10.53, -17.09) * mm, "end": v(10.65, -17.05) * mm});
            skPoint(sketch, "E11.22.0", {"position": v(12.25, -14.6) * mm});
            skPoint(sketch, "E11.22.1", {"position": v(13.47, -13.47) * mm});
            skArc(sketch, "E11.22.2", {"start": v(12.29, -14.62) * mm, "mid": v(12.74, -14.83) * mm, "end": v(13.2, -15) * mm});
            skLineSegment(sketch, "E11.22.3", {"start": v(12.21, -14.56) * mm, "end": v(11.5, -13.71) * mm});
            skLineSegment(sketch, "E11.22.4", {"start": v(13.44, -13.44) * mm, "end": v(12.66, -12.66) * mm});
            skArc(sketch, "E11.22.5", {"start": v(13.49, -13.51) * mm, "mid": v(13.66, -13.98) * mm, "end": v(13.79, -14.47) * mm});
            skPoint(sketch, "E11.22.6", {"position": v(13.35, -15.03) * mm});
            skPoint(sketch, "E11.22.7", {"position": v(13.81, -14.6) * mm});
            skArc(sketch, "E11.22.8", {"start": v(13.71, -14.7) * mm, "mid": v(13.78, -14.6) * mm, "end": v(13.79, -14.47) * mm});
            skArc(sketch, "E11.22.9", {"start": v(13.45, -14.94) * mm, "mid": v(13.52, -14.88) * mm, "end": v(13.58, -14.82) * mm});
            skArc(sketch, "E11.22.10", {"start": v(13.49, -13.51) * mm, "mid": v(13.47, -13.47) * mm, "end": v(13.44, -13.44) * mm});
            skArc(sketch, "E11.22.11", {"start": v(12.21, -14.56) * mm, "mid": v(12.25, -14.6) * mm, "end": v(12.29, -14.62) * mm});
            skArc(sketch, "E11.22.12", {"start": v(13.71, -14.7) * mm, "mid": v(13.65, -14.76) * mm, "end": v(13.58, -14.82) * mm});
            skArc(sketch, "E11.22.13", {"start": v(13.2, -15) * mm, "mid": v(13.34, -15) * mm, "end": v(13.45, -14.94) * mm});
            skPoint(sketch, "E11.23.0", {"position": v(14.6, -12.25) * mm});
            skPoint(sketch, "E11.23.1", {"position": v(15.6, -10.93) * mm});
            skArc(sketch, "E11.23.2", {"start": v(14.64, -12.26) * mm, "mid": v(15.12, -12.4) * mm, "end": v(15.61, -12.47) * mm});
            skLineSegment(sketch, "E11.23.3", {"start": v(14.56, -12.21) * mm, "end": v(13.71, -11.5) * mm});
            skLineSegment(sketch, "E11.23.4", {"start": v(15.57, -10.9) * mm, "end": v(14.66, -10.27) * mm});
            skArc(sketch, "E11.23.5", {"start": v(15.63, -10.97) * mm, "mid": v(15.88, -11.4) * mm, "end": v(16.1, -11.85) * mm});
            skPoint(sketch, "E11.23.6", {"position": v(15.76, -12.49) * mm});
            skPoint(sketch, "E11.23.7", {"position": v(16.14, -11.99) * mm});
            skArc(sketch, "E11.23.8", {"start": v(16.06, -12.1) * mm, "mid": v(16.1, -11.98) * mm, "end": v(16.1, -11.85) * mm});
            skArc(sketch, "E11.23.9", {"start": v(15.84, -12.38) * mm, "mid": v(15.9, -12.3) * mm, "end": v(15.95, -12.24) * mm});
            skArc(sketch, "E11.23.10", {"start": v(15.63, -10.97) * mm, "mid": v(15.6, -10.93) * mm, "end": v(15.57, -10.9) * mm});
            skArc(sketch, "E11.23.11", {"start": v(14.56, -12.21) * mm, "mid": v(14.6, -12.24) * mm, "end": v(14.64, -12.26) * mm});
            skArc(sketch, "E11.23.12", {"start": v(16.06, -12.1) * mm, "mid": v(16, -12.17) * mm, "end": v(15.95, -12.24) * mm});
            skArc(sketch, "E11.23.13", {"start": v(15.61, -12.47) * mm, "mid": v(15.74, -12.46) * mm, "end": v(15.84, -12.38) * mm});
            skPoint(sketch, "E11.24.0", {"position": v(16.5, -9.52) * mm});
            skPoint(sketch, "E11.24.1", {"position": v(17.27, -8.05) * mm});
            skArc(sketch, "E11.24.2", {"start": v(16.55, -9.53) * mm, "mid": v(17.04, -9.58) * mm, "end": v(17.54, -9.57) * mm});
            skLineSegment(sketch, "E11.24.3", {"start": v(16.46, -9.5) * mm, "end": v(15.5, -8.95) * mm});
            skLineSegment(sketch, "E11.24.4", {"start": v(17.22, -8.03) * mm, "end": v(16.22, -7.57) * mm});
            skArc(sketch, "E11.24.5", {"start": v(17.3, -8.09) * mm, "mid": v(17.62, -8.47) * mm, "end": v(17.9, -8.88) * mm});
            skPoint(sketch, "E11.24.6", {"position": v(17.68, -9.56) * mm});
            skPoint(sketch, "E11.24.7", {"position": v(17.98, -9) * mm});
            skArc(sketch, "E11.24.8", {"start": v(17.91, -9.13) * mm, "mid": v(17.94, -9) * mm, "end": v(17.9, -8.88) * mm});
            skArc(sketch, "E11.24.9", {"start": v(17.75, -9.44) * mm, "mid": v(17.8, -9.36) * mm, "end": v(17.83, -9.28) * mm});
            skArc(sketch, "E11.24.10", {"start": v(17.3, -8.09) * mm, "mid": v(17.26, -8.05) * mm, "end": v(17.22, -8.03) * mm});
            skArc(sketch, "E11.24.11", {"start": v(16.46, -9.5) * mm, "mid": v(16.5, -9.52) * mm, "end": v(16.55, -9.53) * mm});
            skArc(sketch, "E11.24.12", {"start": v(17.91, -9.13) * mm, "mid": v(17.87, -9.2) * mm, "end": v(17.83, -9.28) * mm});
            skArc(sketch, "E11.24.13", {"start": v(17.54, -9.57) * mm, "mid": v(17.66, -9.53) * mm, "end": v(17.75, -9.44) * mm});
            skPoint(sketch, "E11.25.0", {"position": v(17.9, -6.52) * mm});
            skPoint(sketch, "E11.25.1", {"position": v(18.4, -4.93) * mm});
            skArc(sketch, "E11.25.2", {"start": v(17.95, -6.51) * mm, "mid": v(18.45, -6.47) * mm, "end": v(18.94, -6.38) * mm});
            skLineSegment(sketch, "E11.25.3", {"start": v(17.86, -6.5) * mm, "end": v(16.82, -6.12) * mm});
            skLineSegment(sketch, "E11.25.4", {"start": v(18.36, -4.92) * mm, "end": v(17.3, -4.63) * mm});
            skArc(sketch, "E11.25.5", {"start": v(18.44, -4.96) * mm, "mid": v(18.82, -5.28) * mm, "end": v(19.17, -5.63) * mm});
            skPoint(sketch, "E11.25.6", {"position": v(19.08, -6.35) * mm});
            skPoint(sketch, "E11.25.7", {"position": v(19.27, -5.74) * mm});
            skArc(sketch, "E11.25.8", {"start": v(19.23, -5.88) * mm, "mid": v(19.23, -5.75) * mm, "end": v(19.17, -5.63) * mm});
            skArc(sketch, "E11.25.9", {"start": v(19.12, -6.21) * mm, "mid": v(19.15, -6.13) * mm, "end": v(19.17, -6.05) * mm});
            skArc(sketch, "E11.25.10", {"start": v(18.44, -4.96) * mm, "mid": v(18.4, -4.93) * mm, "end": v(18.36, -4.92) * mm});
            skArc(sketch, "E11.25.11", {"start": v(17.86, -6.5) * mm, "mid": v(17.9, -6.51) * mm, "end": v(17.95, -6.51) * mm});
            skArc(sketch, "E11.25.12", {"start": v(19.23, -5.88) * mm, "mid": v(19.2, -5.96) * mm, "end": v(19.17, -6.05) * mm});
            skArc(sketch, "E11.25.13", {"start": v(18.94, -6.38) * mm, "mid": v(19.05, -6.32) * mm, "end": v(19.12, -6.21) * mm});
            skPoint(sketch, "E11.26.0", {"position": v(18.76, -3.3) * mm});
            skPoint(sketch, "E11.26.1", {"position": v(18.98, -1.66) * mm});
            skArc(sketch, "E11.26.2", {"start": v(18.8, -3.3) * mm, "mid": v(19.3, -3.17) * mm, "end": v(19.76, -3) * mm});
            skLineSegment(sketch, "E11.26.3", {"start": v(18.71, -3.3) * mm, "end": v(17.63, -3.1) * mm});
            skLineSegment(sketch, "E11.26.4", {"start": v(18.93, -1.66) * mm, "end": v(17.83, -1.56) * mm});
            skArc(sketch, "E11.26.5", {"start": v(19.02, -1.68) * mm, "mid": v(19.46, -1.93) * mm, "end": v(19.86, -2.22) * mm});
            skPoint(sketch, "E11.26.6", {"position": v(19.89, -2.94) * mm});
            skPoint(sketch, "E11.26.7", {"position": v(19.97, -2.31) * mm});
            skArc(sketch, "E11.26.8", {"start": v(19.95, -2.45) * mm, "mid": v(19.94, -2.32) * mm, "end": v(19.86, -2.22) * mm});
            skArc(sketch, "E11.26.9", {"start": v(19.9, -2.8) * mm, "mid": v(19.92, -2.71) * mm, "end": v(19.93, -2.62) * mm});
            skArc(sketch, "E11.26.10", {"start": v(19.02, -1.68) * mm, "mid": v(18.98, -1.66) * mm, "end": v(18.93, -1.66) * mm});
            skArc(sketch, "E11.26.11", {"start": v(18.71, -3.3) * mm, "mid": v(18.76, -3.3) * mm, "end": v(18.8, -3.3) * mm});
            skArc(sketch, "E11.26.12", {"start": v(19.95, -2.45) * mm, "mid": v(19.94, -2.54) * mm, "end": v(19.93, -2.62) * mm});
            skArc(sketch, "E11.26.13", {"start": v(19.76, -3) * mm, "mid": v(19.86, -2.92) * mm, "end": v(19.9, -2.8) * mm});
            skPoint(sketch, "E11.27.0", {"position": v(19.05, 0) * mm});
            skPoint(sketch, "E11.27.1", {"position": v(18.98, 1.66) * mm});
            skArc(sketch, "E11.27.2", {"start": v(19.1, 0.02) * mm, "mid": v(19.55, 0.23) * mm, "end": v(19.98, 0.48) * mm});
            skLineSegment(sketch, "E11.27.3", {"start": v(19, 0) * mm, "end": v(17.9, 0) * mm});
            skLineSegment(sketch, "E11.27.4", {"start": v(18.93, 1.66) * mm, "end": v(17.83, 1.56) * mm});
            skArc(sketch, "E11.27.5", {"start": v(19.02, 1.65) * mm, "mid": v(19.5, 1.48) * mm, "end": v(19.94, 1.26) * mm});
            skPoint(sketch, "E11.27.6", {"position": v(20.1, 0.56) * mm});
            skPoint(sketch, "E11.27.7", {"position": v(20.07, 1.2) * mm});
            skArc(sketch, "E11.27.8", {"start": v(20.08, 1.05) * mm, "mid": v(20.04, 1.18) * mm, "end": v(19.94, 1.26) * mm});
            skArc(sketch, "E11.27.9", {"start": v(20.1, 0.7) * mm, "mid": v(20.09, 0.79) * mm, "end": v(20.08, 0.88) * mm});
            skArc(sketch, "E11.27.10", {"start": v(19.02, 1.65) * mm, "mid": v(18.98, 1.66) * mm, "end": v(18.93, 1.66) * mm});
            skArc(sketch, "E11.27.11", {"start": v(19, 0) * mm, "mid": v(19.05, 0) * mm, "end": v(19.1, 0.02) * mm});
            skArc(sketch, "E11.27.12", {"start": v(20.08, 1.05) * mm, "mid": v(20.08, 0.97) * mm, "end": v(20.08, 0.88) * mm});
            skArc(sketch, "E11.27.13", {"start": v(19.98, 0.48) * mm, "mid": v(20.06, 0.58) * mm, "end": v(20.1, 0.7) * mm});
            skPoint(sketch, "E11.28.0", {"position": v(18.76, 3.3) * mm});
            skPoint(sketch, "E11.28.1", {"position": v(18.4, 4.93) * mm});
            skArc(sketch, "E11.28.2", {"start": v(18.8, 3.33) * mm, "mid": v(19.21, 3.62) * mm, "end": v(19.6, 3.94) * mm});
            skLineSegment(sketch, "E11.28.3", {"start": v(18.71, 3.3) * mm, "end": v(17.63, 3.1) * mm});
            skLineSegment(sketch, "E11.28.4", {"start": v(18.36, 4.92) * mm, "end": v(17.3, 4.63) * mm});
            skArc(sketch, "E11.28.5", {"start": v(18.45, 4.93) * mm, "mid": v(18.94, 4.84) * mm, "end": v(19.42, 4.7) * mm});
            skPoint(sketch, "E11.28.6", {"position": v(19.7, 4.04) * mm});
            skPoint(sketch, "E11.28.7", {"position": v(19.56, 4.66) * mm});
            skArc(sketch, "E11.28.8", {"start": v(19.59, 4.52) * mm, "mid": v(19.53, 4.64) * mm, "end": v(19.42, 4.7) * mm});
            skArc(sketch, "E11.28.9", {"start": v(19.67, 4.18) * mm, "mid": v(19.65, 4.27) * mm, "end": v(19.63, 4.35) * mm});
            skArc(sketch, "E11.28.10", {"start": v(18.45, 4.93) * mm, "mid": v(18.4, 4.93) * mm, "end": v(18.36, 4.92) * mm});
            skArc(sketch, "E11.28.11", {"start": v(18.71, 3.3) * mm, "mid": v(18.76, 3.31) * mm, "end": v(18.8, 3.33) * mm});
            skArc(sketch, "E11.28.12", {"start": v(19.59, 4.52) * mm, "mid": v(19.6, 4.44) * mm, "end": v(19.63, 4.35) * mm});
            skArc(sketch, "E11.28.13", {"start": v(19.6, 3.94) * mm, "mid": v(19.66, 4.05) * mm, "end": v(19.67, 4.18) * mm});
            skPoint(sketch, "E11.29.0", {"position": v(17.9, 6.52) * mm});
            skPoint(sketch, "E11.29.1", {"position": v(17.27, 8.05) * mm});
            skArc(sketch, "E11.29.2", {"start": v(17.94, 6.55) * mm, "mid": v(18.3, 6.9) * mm, "end": v(18.6, 7.28) * mm});
            skLineSegment(sketch, "E11.29.3", {"start": v(17.86, 6.5) * mm, "end": v(16.82, 6.12) * mm});
            skLineSegment(sketch, "E11.29.4", {"start": v(17.22, 8.03) * mm, "end": v(16.22, 7.57) * mm});
            skArc(sketch, "E11.29.5", {"start": v(17.31, 8.05) * mm, "mid": v(17.81, 8.06) * mm, "end": v(18.3, 8) * mm});
            skPoint(sketch, "E11.29.6", {"position": v(18.7, 7.4) * mm});
            skPoint(sketch, "E11.29.7", {"position": v(18.45, 7.98) * mm});
            skArc(sketch, "E11.29.8", {"start": v(18.5, 7.86) * mm, "mid": v(18.43, 7.96) * mm, "end": v(18.3, 8) * mm});
            skArc(sketch, "E11.29.9", {"start": v(18.64, 7.53) * mm, "mid": v(18.6, 7.61) * mm, "end": v(18.57, 7.7) * mm});
            skArc(sketch, "E11.29.10", {"start": v(17.31, 8.05) * mm, "mid": v(17.27, 8.05) * mm, "end": v(17.22, 8.03) * mm});
            skArc(sketch, "E11.29.11", {"start": v(17.86, 6.5) * mm, "mid": v(17.9, 6.52) * mm, "end": v(17.94, 6.55) * mm});
            skArc(sketch, "E11.29.12", {"start": v(18.5, 7.86) * mm, "mid": v(18.54, 7.78) * mm, "end": v(18.57, 7.7) * mm});
            skArc(sketch, "E11.29.13", {"start": v(18.6, 7.28) * mm, "mid": v(18.66, 7.4) * mm, "end": v(18.64, 7.53) * mm});
            skPoint(sketch, "E11.30.0", {"position": v(16.5, 9.52) * mm});
            skPoint(sketch, "E11.30.1", {"position": v(15.6, 10.93) * mm});
            skArc(sketch, "E11.30.2", {"start": v(16.53, 9.56) * mm, "mid": v(16.82, 9.97) * mm, "end": v(17.06, 10.4) * mm});
            skLineSegment(sketch, "E11.30.3", {"start": v(16.46, 9.5) * mm, "end": v(15.5, 8.95) * mm});
            skLineSegment(sketch, "E11.30.4", {"start": v(15.57, 10.9) * mm, "end": v(14.66, 10.27) * mm});
            skArc(sketch, "E11.30.5", {"start": v(15.65, 10.94) * mm, "mid": v(16.14, 11.03) * mm, "end": v(16.64, 11.07) * mm});
            skPoint(sketch, "E11.30.6", {"position": v(17.12, 10.53) * mm});
            skPoint(sketch, "E11.30.7", {"position": v(16.78, 11.07) * mm});
            skArc(sketch, "E11.30.8", {"start": v(16.86, 10.95) * mm, "mid": v(16.77, 11.04) * mm, "end": v(16.64, 11.07) * mm});
            skArc(sketch, "E11.30.9", {"start": v(17.05, 10.65) * mm, "mid": v(17, 10.73) * mm, "end": v(16.96, 10.8) * mm});
            skArc(sketch, "E11.30.10", {"start": v(15.65, 10.94) * mm, "mid": v(15.6, 10.92) * mm, "end": v(15.57, 10.9) * mm});
            skArc(sketch, "E11.30.11", {"start": v(16.46, 9.5) * mm, "mid": v(16.5, 9.53) * mm, "end": v(16.53, 9.56) * mm});
            skArc(sketch, "E11.30.12", {"start": v(16.86, 10.95) * mm, "mid": v(16.9, 10.88) * mm, "end": v(16.96, 10.8) * mm});
            skArc(sketch, "E11.30.13", {"start": v(17.06, 10.4) * mm, "mid": v(17.09, 10.53) * mm, "end": v(17.05, 10.65) * mm});
            skPoint(sketch, "E11.31.0", {"position": v(14.6, 12.25) * mm});
            skPoint(sketch, "E11.31.1", {"position": v(13.47, 13.47) * mm});
            skArc(sketch, "E11.31.2", {"start": v(14.62, 12.29) * mm, "mid": v(14.83, 12.74) * mm, "end": v(15, 13.2) * mm});
            skLineSegment(sketch, "E11.31.3", {"start": v(14.56, 12.21) * mm, "end": v(13.71, 11.5) * mm});
            skLineSegment(sketch, "E11.31.4", {"start": v(13.44, 13.44) * mm, "end": v(12.66, 12.66) * mm});
            skArc(sketch, "E11.31.5", {"start": v(13.51, 13.49) * mm, "mid": v(13.98, 13.66) * mm, "end": v(14.47, 13.79) * mm});
            skPoint(sketch, "E11.31.6", {"position": v(15.03, 13.35) * mm});
            skPoint(sketch, "E11.31.7", {"position": v(14.6, 13.81) * mm});
            skArc(sketch, "E11.31.8", {"start": v(14.7, 13.71) * mm, "mid": v(14.6, 13.78) * mm, "end": v(14.47, 13.79) * mm});
            skArc(sketch, "E11.31.9", {"start": v(14.94, 13.45) * mm, "mid": v(14.88, 13.52) * mm, "end": v(14.82, 13.58) * mm});
            skArc(sketch, "E11.31.10", {"start": v(13.51, 13.49) * mm, "mid": v(13.47, 13.47) * mm, "end": v(13.44, 13.44) * mm});
            skArc(sketch, "E11.31.11", {"start": v(14.56, 12.21) * mm, "mid": v(14.6, 12.25) * mm, "end": v(14.62, 12.29) * mm});
            skArc(sketch, "E11.31.12", {"start": v(14.7, 13.71) * mm, "mid": v(14.76, 13.65) * mm, "end": v(14.82, 13.58) * mm});
            skArc(sketch, "E11.31.13", {"start": v(15, 13.2) * mm, "mid": v(15, 13.34) * mm, "end": v(14.94, 13.45) * mm});
            skPoint(sketch, "E11.32.0", {"position": v(12.25, 14.6) * mm});
            skPoint(sketch, "E11.32.1", {"position": v(10.93, 15.6) * mm});
            skArc(sketch, "E11.32.2", {"start": v(12.26, 14.64) * mm, "mid": v(12.4, 15.12) * mm, "end": v(12.47, 15.61) * mm});
            skLineSegment(sketch, "E11.32.3", {"start": v(12.21, 14.56) * mm, "end": v(11.5, 13.71) * mm});
            skLineSegment(sketch, "E11.32.4", {"start": v(10.9, 15.57) * mm, "end": v(10.27, 14.66) * mm});
            skArc(sketch, "E11.32.5", {"start": v(10.97, 15.63) * mm, "mid": v(11.4, 15.88) * mm, "end": v(11.85, 16.1) * mm});
            skPoint(sketch, "E11.32.6", {"position": v(12.49, 15.76) * mm});
            skPoint(sketch, "E11.32.7", {"position": v(11.99, 16.14) * mm});
            skArc(sketch, "E11.32.8", {"start": v(12.1, 16.06) * mm, "mid": v(11.98, 16.1) * mm, "end": v(11.85, 16.1) * mm});
            skArc(sketch, "E11.32.9", {"start": v(12.38, 15.84) * mm, "mid": v(12.3, 15.9) * mm, "end": v(12.24, 15.95) * mm});
            skArc(sketch, "E11.32.10", {"start": v(10.97, 15.63) * mm, "mid": v(10.93, 15.6) * mm, "end": v(10.9, 15.57) * mm});
            skArc(sketch, "E11.32.11", {"start": v(12.21, 14.56) * mm, "mid": v(12.24, 14.6) * mm, "end": v(12.26, 14.64) * mm});
            skArc(sketch, "E11.32.12", {"start": v(12.1, 16.06) * mm, "mid": v(12.17, 16) * mm, "end": v(12.24, 15.95) * mm});
            skArc(sketch, "E11.32.13", {"start": v(12.47, 15.61) * mm, "mid": v(12.46, 15.74) * mm, "end": v(12.38, 15.84) * mm});
            skPoint(sketch, "E11.33.0", {"position": v(9.52, 16.5) * mm});
            skPoint(sketch, "E11.33.1", {"position": v(8.05, 17.27) * mm});
            skArc(sketch, "E11.33.2", {"start": v(9.53, 16.55) * mm, "mid": v(9.58, 17.04) * mm, "end": v(9.57, 17.54) * mm});
            skLineSegment(sketch, "E11.33.3", {"start": v(9.5, 16.46) * mm, "end": v(8.95, 15.5) * mm});
            skLineSegment(sketch, "E11.33.4", {"start": v(8.03, 17.22) * mm, "end": v(7.57, 16.22) * mm});
            skArc(sketch, "E11.33.5", {"start": v(8.09, 17.3) * mm, "mid": v(8.47, 17.62) * mm, "end": v(8.88, 17.9) * mm});
            skPoint(sketch, "E11.33.6", {"position": v(9.56, 17.68) * mm});
            skPoint(sketch, "E11.33.7", {"position": v(9, 17.98) * mm});
            skArc(sketch, "E11.33.8", {"start": v(9.13, 17.91) * mm, "mid": v(9, 17.94) * mm, "end": v(8.88, 17.9) * mm});
            skArc(sketch, "E11.33.9", {"start": v(9.44, 17.75) * mm, "mid": v(9.36, 17.8) * mm, "end": v(9.28, 17.83) * mm});
            skArc(sketch, "E11.33.10", {"start": v(8.09, 17.3) * mm, "mid": v(8.05, 17.26) * mm, "end": v(8.03, 17.22) * mm});
            skArc(sketch, "E11.33.11", {"start": v(9.5, 16.46) * mm, "mid": v(9.52, 16.5) * mm, "end": v(9.53, 16.55) * mm});
            skArc(sketch, "E11.33.12", {"start": v(9.13, 17.91) * mm, "mid": v(9.2, 17.87) * mm, "end": v(9.28, 17.83) * mm});
            skArc(sketch, "E11.33.13", {"start": v(9.57, 17.54) * mm, "mid": v(9.53, 17.66) * mm, "end": v(9.44, 17.75) * mm});
            skPoint(sketch, "E11.34.0", {"position": v(6.52, 17.9) * mm});
            skPoint(sketch, "E11.34.1", {"position": v(4.93, 18.4) * mm});
            skArc(sketch, "E11.34.2", {"start": v(6.51, 17.95) * mm, "mid": v(6.47, 18.45) * mm, "end": v(6.38, 18.94) * mm});
            skLineSegment(sketch, "E11.34.3", {"start": v(6.5, 17.86) * mm, "end": v(6.12, 16.82) * mm});
            skLineSegment(sketch, "E11.34.4", {"start": v(4.92, 18.36) * mm, "end": v(4.63, 17.3) * mm});
            skArc(sketch, "E11.34.5", {"start": v(4.96, 18.44) * mm, "mid": v(5.28, 18.82) * mm, "end": v(5.63, 19.17) * mm});
            skPoint(sketch, "E11.34.6", {"position": v(6.35, 19.08) * mm});
            skPoint(sketch, "E11.34.7", {"position": v(5.74, 19.27) * mm});
            skArc(sketch, "E11.34.8", {"start": v(5.88, 19.23) * mm, "mid": v(5.75, 19.23) * mm, "end": v(5.63, 19.17) * mm});
            skArc(sketch, "E11.34.9", {"start": v(6.21, 19.12) * mm, "mid": v(6.13, 19.15) * mm, "end": v(6.05, 19.17) * mm});
            skArc(sketch, "E11.34.10", {"start": v(4.96, 18.44) * mm, "mid": v(4.93, 18.4) * mm, "end": v(4.92, 18.36) * mm});
            skArc(sketch, "E11.34.11", {"start": v(6.5, 17.86) * mm, "mid": v(6.51, 17.9) * mm, "end": v(6.51, 17.95) * mm});
            skArc(sketch, "E11.34.12", {"start": v(5.88, 19.23) * mm, "mid": v(5.96, 19.2) * mm, "end": v(6.05, 19.17) * mm});
            skArc(sketch, "E11.34.13", {"start": v(6.38, 18.94) * mm, "mid": v(6.32, 19.05) * mm, "end": v(6.21, 19.12) * mm});
            skPoint(sketch, "E11.35.0", {"position": v(3.3, 18.76) * mm});
            skPoint(sketch, "E11.35.1", {"position": v(1.66, 18.98) * mm});
            skArc(sketch, "E11.35.2", {"start": v(3.3, 18.8) * mm, "mid": v(3.17, 19.3) * mm, "end": v(3, 19.76) * mm});
            skLineSegment(sketch, "E11.35.3", {"start": v(3.3, 18.71) * mm, "end": v(3.1, 17.63) * mm});
            skLineSegment(sketch, "E11.35.4", {"start": v(1.66, 18.93) * mm, "end": v(1.56, 17.83) * mm});
            skArc(sketch, "E11.35.5", {"start": v(1.68, 19.02) * mm, "mid": v(1.93, 19.46) * mm, "end": v(2.22, 19.86) * mm});
            skPoint(sketch, "E11.35.6", {"position": v(2.94, 19.89) * mm});
            skPoint(sketch, "E11.35.7", {"position": v(2.31, 19.97) * mm});
            skArc(sketch, "E11.35.8", {"start": v(2.45, 19.95) * mm, "mid": v(2.32, 19.94) * mm, "end": v(2.22, 19.86) * mm});
            skArc(sketch, "E11.35.9", {"start": v(2.8, 19.9) * mm, "mid": v(2.71, 19.92) * mm, "end": v(2.62, 19.93) * mm});
            skArc(sketch, "E11.35.10", {"start": v(1.68, 19.02) * mm, "mid": v(1.66, 18.98) * mm, "end": v(1.66, 18.93) * mm});
            skArc(sketch, "E11.35.11", {"start": v(3.3, 18.71) * mm, "mid": v(3.3, 18.76) * mm, "end": v(3.3, 18.8) * mm});
            skArc(sketch, "E11.35.12", {"start": v(2.45, 19.95) * mm, "mid": v(2.54, 19.94) * mm, "end": v(2.62, 19.93) * mm});
            skArc(sketch, "E11.35.13", {"start": v(3, 19.76) * mm, "mid": v(2.92, 19.86) * mm, "end": v(2.8, 19.9) * mm});
            skSolve(sketch);
        }
        {
            var Q0;
            Q0 = qSketchRegion(id + "F0", true);
            var Q1;
            {var subQ0=sQuery(id+"F0.wireOp",EDGE,"E1");var subQ39=makeQuery(id+"F0.imprint","INTERSECT",VERTEX,{"derivedFrom":[subQ0,sQuery(id+"F0.wireOp",EDGE,"E11.27.3")]});Q1=makeQuery(id+"F0.imprint","IMPRINT",FACE,{"disambiguationData":[TD([[makeQuery(id+"F0.imprint","IMPRINT",EDGE,{"disambiguationData":[TD([[subQ39,-1.0]])],"derivedFrom":subQ0}),1.0]])]});}
            extrude(context, id + "F1", {"entities" : qUnion([Q0, Q1]), "depth" : 6.35 * mm});
        }
        {
            var Q0;
            Q0=makeQuery(id+"F1.opExtrude","CAP_FACE",FACE,{"disambiguationData":[OSD([sQuery(id+"F0.wireOp",EDGE,"E0"),sQuery(id+"F0.wireOp",EDGE,"E1"),sQuery(id+"F0.wireOp",EDGE,"E2.trimOffspring"),sQuery(id+"F0.wireOp",EDGE,"E3"),sQuery(id+"F0.wireOp",EDGE,"E4.MirrorCS"),sQuery(id+"F0.wireOp",EDGE,"E5.MirrorCS"),sQuery(id+"F0.wireOp",EDGE,"E6.MirrorCS"),sQuery(id+"F0.wireOp",EDGE,"E7.filletArc"),sQuery(id+"F0.wireOp",EDGE,"E8.filletArc"),sQuery(id+"F0.wireOp",EDGE,"E9.filletArc"),sQuery(id+"F0.wireOp",EDGE,"E10.filletArc"),sQuery(id+"F0.wireOp",EDGE,"E11.1.2"),sQuery(id+"F0.wireOp",EDGE,"E11.1.3"),sQuery(id+"F0.wireOp",EDGE,"E11.1.4"),sQuery(id+"F0.wireOp",EDGE,"E11.1.5"),sQuery(id+"F0.wireOp",EDGE,"E11.1.8"),sQuery(id+"F0.wireOp",EDGE,"E11.1.9"),sQuery(id+"F0.wireOp",EDGE,"E11.1.10"),sQuery(id+"F0.wireOp",EDGE,"E11.1.11"),sQuery(id+"F0.wireOp",EDGE,"E11.1.12"),sQuery(id+"F0.wireOp",EDGE,"E11.1.13"),sQuery(id+"F0.wireOp",EDGE,"E11.2.2"),sQuery(id+"F0.wireOp",EDGE,"E11.2.3"),sQuery(id+"F0.wireOp",EDGE,"E11.2.4"),sQuery(id+"F0.wireOp",EDGE,"E11.2.5"),sQuery(id+"F0.wireOp",EDGE,"E11.2.8"),sQuery(id+"F0.wireOp",EDGE,"E11.2.9"),sQuery(id+"F0.wireOp",EDGE,"E11.2.10"),sQuery(id+"F0.wireOp",EDGE,"E11.2.11"),sQuery(id+"F0.wireOp",EDGE,"E11.2.12"),sQuery(id+"F0.wireOp",EDGE,"E11.2.13"),sQuery(id+"F0.wireOp",EDGE,"E11.3.2"),sQuery(id+"F0.wireOp",EDGE,"E11.3.3"),sQuery(id+"F0.wireOp",EDGE,"E11.3.4"),sQuery(id+"F0.wireOp",EDGE,"E11.3.5"),sQuery(id+"F0.wireOp",EDGE,"E11.3.8"),sQuery(id+"F0.wireOp",EDGE,"E11.3.9"),sQuery(id+"F0.wireOp",EDGE,"E11.3.10"),sQuery(id+"F0.wireOp",EDGE,"E11.3.11"),sQuery(id+"F0.wireOp",EDGE,"E11.3.12"),sQuery(id+"F0.wireOp",EDGE,"E11.3.13"),sQuery(id+"F0.wireOp",EDGE,"E11.4.2"),sQuery(id+"F0.wireOp",EDGE,"E11.4.3"),sQuery(id+"F0.wireOp",EDGE,"E11.4.4"),sQuery(id+"F0.wireOp",EDGE,"E11.4.5"),sQuery(id+"F0.wireOp",EDGE,"E11.4.8"),sQuery(id+"F0.wireOp",EDGE,"E11.4.9"),sQuery(id+"F0.wireOp",EDGE,"E11.4.10"),sQuery(id+"F0.wireOp",EDGE,"E11.4.11"),sQuery(id+"F0.wireOp",EDGE,"E11.4.12"),sQuery(id+"F0.wireOp",EDGE,"E11.4.13"),sQuery(id+"F0.wireOp",EDGE,"E11.5.2"),sQuery(id+"F0.wireOp",EDGE,"E11.5.3"),sQuery(id+"F0.wireOp",EDGE,"E11.5.4"),sQuery(id+"F0.wireOp",EDGE,"E11.5.5"),sQuery(id+"F0.wireOp",EDGE,"E11.5.8"),sQuery(id+"F0.wireOp",EDGE,"E11.5.9"),sQuery(id+"F0.wireOp",EDGE,"E11.5.10"),sQuery(id+"F0.wireOp",EDGE,"E11.5.11"),sQuery(id+"F0.wireOp",EDGE,"E11.5.12"),sQuery(id+"F0.wireOp",EDGE,"E11.5.13"),sQuery(id+"F0.wireOp",EDGE,"E11.6.2"),sQuery(id+"F0.wireOp",EDGE,"E11.6.3"),sQuery(id+"F0.wireOp",EDGE,"E11.6.4"),sQuery(id+"F0.wireOp",EDGE,"E11.6.5"),sQuery(id+"F0.wireOp",EDGE,"E11.6.8"),sQuery(id+"F0.wireOp",EDGE,"E11.6.9"),sQuery(id+"F0.wireOp",EDGE,"E11.6.10"),sQuery(id+"F0.wireOp",EDGE,"E11.6.11"),sQuery(id+"F0.wireOp",EDGE,"E11.6.12"),sQuery(id+"F0.wireOp",EDGE,"E11.6.13"),sQuery(id+"F0.wireOp",EDGE,"E11.7.2"),sQuery(id+"F0.wireOp",EDGE,"E11.7.3"),sQuery(id+"F0.wireOp",EDGE,"E11.7.4"),sQuery(id+"F0.wireOp",EDGE,"E11.7.5"),sQuery(id+"F0.wireOp",EDGE,"E11.7.8"),sQuery(id+"F0.wireOp",EDGE,"E11.7.9"),sQuery(id+"F0.wireOp",EDGE,"E11.7.10"),sQuery(id+"F0.wireOp",EDGE,"E11.7.11"),sQuery(id+"F0.wireOp",EDGE,"E11.7.12"),sQuery(id+"F0.wireOp",EDGE,"E11.7.13"),sQuery(id+"F0.wireOp",EDGE,"E11.8.2"),sQuery(id+"F0.wireOp",EDGE,"E11.8.3"),sQuery(id+"F0.wireOp",EDGE,"E11.8.4"),sQuery(id+"F0.wireOp",EDGE,"E11.8.5"),sQuery(id+"F0.wireOp",EDGE,"E11.8.8"),sQuery(id+"F0.wireOp",EDGE,"E11.8.9"),sQuery(id+"F0.wireOp",EDGE,"E11.8.10"),sQuery(id+"F0.wireOp",EDGE,"E11.8.11"),sQuery(id+"F0.wireOp",EDGE,"E11.8.12"),sQuery(id+"F0.wireOp",EDGE,"E11.8.13"),sQuery(id+"F0.wireOp",EDGE,"E11.9.2"),sQuery(id+"F0.wireOp",EDGE,"E11.9.3"),sQuery(id+"F0.wireOp",EDGE,"E11.9.4"),sQuery(id+"F0.wireOp",EDGE,"E11.9.5"),sQuery(id+"F0.wireOp",EDGE,"E11.9.8"),sQuery(id+"F0.wireOp",EDGE,"E11.9.9"),sQuery(id+"F0.wireOp",EDGE,"E11.9.10"),sQuery(id+"F0.wireOp",EDGE,"E11.9.11"),sQuery(id+"F0.wireOp",EDGE,"E11.9.12"),sQuery(id+"F0.wireOp",EDGE,"E11.9.13"),sQuery(id+"F0.wireOp",EDGE,"E11.10.2"),sQuery(id+"F0.wireOp",EDGE,"E11.10.3"),sQuery(id+"F0.wireOp",EDGE,"E11.10.4"),sQuery(id+"F0.wireOp",EDGE,"E11.10.5"),sQuery(id+"F0.wireOp",EDGE,"E11.10.8"),sQuery(id+"F0.wireOp",EDGE,"E11.10.9"),sQuery(id+"F0.wireOp",EDGE,"E11.10.10"),sQuery(id+"F0.wireOp",EDGE,"E11.10.11"),sQuery(id+"F0.wireOp",EDGE,"E11.10.12"),sQuery(id+"F0.wireOp",EDGE,"E11.10.13"),sQuery(id+"F0.wireOp",EDGE,"E11.11.2"),sQuery(id+"F0.wireOp",EDGE,"E11.11.3"),sQuery(id+"F0.wireOp",EDGE,"E11.11.4"),sQuery(id+"F0.wireOp",EDGE,"E11.11.5"),sQuery(id+"F0.wireOp",EDGE,"E11.11.8"),sQuery(id+"F0.wireOp",EDGE,"E11.11.9"),sQuery(id+"F0.wireOp",EDGE,"E11.11.10"),sQuery(id+"F0.wireOp",EDGE,"E11.11.11"),sQuery(id+"F0.wireOp",EDGE,"E11.11.12"),sQuery(id+"F0.wireOp",EDGE,"E11.11.13"),sQuery(id+"F0.wireOp",EDGE,"E11.12.2"),sQuery(id+"F0.wireOp",EDGE,"E11.12.3"),sQuery(id+"F0.wireOp",EDGE,"E11.12.4"),sQuery(id+"F0.wireOp",EDGE,"E11.12.5"),sQuery(id+"F0.wireOp",EDGE,"E11.12.8"),sQuery(id+"F0.wireOp",EDGE,"E11.12.9"),sQuery(id+"F0.wireOp",EDGE,"E11.12.10"),sQuery(id+"F0.wireOp",EDGE,"E11.12.11"),sQuery(id+"F0.wireOp",EDGE,"E11.12.12"),sQuery(id+"F0.wireOp",EDGE,"E11.12.13"),sQuery(id+"F0.wireOp",EDGE,"E11.13.2"),sQuery(id+"F0.wireOp",EDGE,"E11.13.3"),sQuery(id+"F0.wireOp",EDGE,"E11.13.4"),sQuery(id+"F0.wireOp",EDGE,"E11.13.5"),sQuery(id+"F0.wireOp",EDGE,"E11.13.8"),sQuery(id+"F0.wireOp",EDGE,"E11.13.9"),sQuery(id+"F0.wireOp",EDGE,"E11.13.10"),sQuery(id+"F0.wireOp",EDGE,"E11.13.11"),sQuery(id+"F0.wireOp",EDGE,"E11.13.12"),sQuery(id+"F0.wireOp",EDGE,"E11.13.13"),sQuery(id+"F0.wireOp",EDGE,"E11.14.2"),sQuery(id+"F0.wireOp",EDGE,"E11.14.3"),sQuery(id+"F0.wireOp",EDGE,"E11.14.4"),sQuery(id+"F0.wireOp",EDGE,"E11.14.5"),sQuery(id+"F0.wireOp",EDGE,"E11.14.8"),sQuery(id+"F0.wireOp",EDGE,"E11.14.9"),sQuery(id+"F0.wireOp",EDGE,"E11.14.10"),sQuery(id+"F0.wireOp",EDGE,"E11.14.11"),sQuery(id+"F0.wireOp",EDGE,"E11.14.12"),sQuery(id+"F0.wireOp",EDGE,"E11.14.13"),sQuery(id+"F0.wireOp",EDGE,"E11.15.2"),sQuery(id+"F0.wireOp",EDGE,"E11.15.3"),sQuery(id+"F0.wireOp",EDGE,"E11.15.4"),sQuery(id+"F0.wireOp",EDGE,"E11.15.5"),sQuery(id+"F0.wireOp",EDGE,"E11.15.8"),sQuery(id+"F0.wireOp",EDGE,"E11.15.9"),sQuery(id+"F0.wireOp",EDGE,"E11.15.10"),sQuery(id+"F0.wireOp",EDGE,"E11.15.11"),sQuery(id+"F0.wireOp",EDGE,"E11.15.12"),sQuery(id+"F0.wireOp",EDGE,"E11.15.13"),sQuery(id+"F0.wireOp",EDGE,"E11.16.2"),sQuery(id+"F0.wireOp",EDGE,"E11.16.3"),sQuery(id+"F0.wireOp",EDGE,"E11.16.4"),sQuery(id+"F0.wireOp",EDGE,"E11.16.5"),sQuery(id+"F0.wireOp",EDGE,"E11.16.8"),sQuery(id+"F0.wireOp",EDGE,"E11.16.9"),sQuery(id+"F0.wireOp",EDGE,"E11.16.10"),sQuery(id+"F0.wireOp",EDGE,"E11.16.11"),sQuery(id+"F0.wireOp",EDGE,"E11.16.12"),sQuery(id+"F0.wireOp",EDGE,"E11.16.13"),sQuery(id+"F0.wireOp",EDGE,"E11.17.2"),sQuery(id+"F0.wireOp",EDGE,"E11.17.3"),sQuery(id+"F0.wireOp",EDGE,"E11.17.4"),sQuery(id+"F0.wireOp",EDGE,"E11.17.5"),sQuery(id+"F0.wireOp",EDGE,"E11.17.8"),sQuery(id+"F0.wireOp",EDGE,"E11.17.9"),sQuery(id+"F0.wireOp",EDGE,"E11.17.10"),sQuery(id+"F0.wireOp",EDGE,"E11.17.11"),sQuery(id+"F0.wireOp",EDGE,"E11.17.12"),sQuery(id+"F0.wireOp",EDGE,"E11.17.13"),sQuery(id+"F0.wireOp",EDGE,"E11.18.2"),sQuery(id+"F0.wireOp",EDGE,"E11.18.3"),sQuery(id+"F0.wireOp",EDGE,"E11.18.4"),sQuery(id+"F0.wireOp",EDGE,"E11.18.5"),sQuery(id+"F0.wireOp",EDGE,"E11.18.8"),sQuery(id+"F0.wireOp",EDGE,"E11.18.9"),sQuery(id+"F0.wireOp",EDGE,"E11.18.10"),sQuery(id+"F0.wireOp",EDGE,"E11.18.11"),sQuery(id+"F0.wireOp",EDGE,"E11.18.12"),sQuery(id+"F0.wireOp",EDGE,"E11.18.13"),sQuery(id+"F0.wireOp",EDGE,"E11.19.2"),sQuery(id+"F0.wireOp",EDGE,"E11.19.3"),sQuery(id+"F0.wireOp",EDGE,"E11.19.4"),sQuery(id+"F0.wireOp",EDGE,"E11.19.5"),sQuery(id+"F0.wireOp",EDGE,"E11.19.8"),sQuery(id+"F0.wireOp",EDGE,"E11.19.9"),sQuery(id+"F0.wireOp",EDGE,"E11.19.10"),sQuery(id+"F0.wireOp",EDGE,"E11.19.11"),sQuery(id+"F0.wireOp",EDGE,"E11.19.12"),sQuery(id+"F0.wireOp",EDGE,"E11.19.13"),sQuery(id+"F0.wireOp",EDGE,"E11.20.2"),sQuery(id+"F0.wireOp",EDGE,"E11.20.3"),sQuery(id+"F0.wireOp",EDGE,"E11.20.4"),sQuery(id+"F0.wireOp",EDGE,"E11.20.5"),sQuery(id+"F0.wireOp",EDGE,"E11.20.8"),sQuery(id+"F0.wireOp",EDGE,"E11.20.9"),sQuery(id+"F0.wireOp",EDGE,"E11.20.10"),sQuery(id+"F0.wireOp",EDGE,"E11.20.11"),sQuery(id+"F0.wireOp",EDGE,"E11.20.12"),sQuery(id+"F0.wireOp",EDGE,"E11.20.13"),sQuery(id+"F0.wireOp",EDGE,"E11.21.2"),sQuery(id+"F0.wireOp",EDGE,"E11.21.3"),sQuery(id+"F0.wireOp",EDGE,"E11.21.4"),sQuery(id+"F0.wireOp",EDGE,"E11.21.5"),sQuery(id+"F0.wireOp",EDGE,"E11.21.8"),sQuery(id+"F0.wireOp",EDGE,"E11.21.9"),sQuery(id+"F0.wireOp",EDGE,"E11.21.10"),sQuery(id+"F0.wireOp",EDGE,"E11.21.11"),sQuery(id+"F0.wireOp",EDGE,"E11.21.12"),sQuery(id+"F0.wireOp",EDGE,"E11.21.13"),sQuery(id+"F0.wireOp",EDGE,"E11.22.2"),sQuery(id+"F0.wireOp",EDGE,"E11.22.3"),sQuery(id+"F0.wireOp",EDGE,"E11.22.4"),sQuery(id+"F0.wireOp",EDGE,"E11.22.5"),sQuery(id+"F0.wireOp",EDGE,"E11.22.8"),sQuery(id+"F0.wireOp",EDGE,"E11.22.9"),sQuery(id+"F0.wireOp",EDGE,"E11.22.10"),sQuery(id+"F0.wireOp",EDGE,"E11.22.11"),sQuery(id+"F0.wireOp",EDGE,"E11.22.12"),sQuery(id+"F0.wireOp",EDGE,"E11.22.13"),sQuery(id+"F0.wireOp",EDGE,"E11.23.2"),sQuery(id+"F0.wireOp",EDGE,"E11.23.3"),sQuery(id+"F0.wireOp",EDGE,"E11.23.4"),sQuery(id+"F0.wireOp",EDGE,"E11.23.5"),sQuery(id+"F0.wireOp",EDGE,"E11.23.8"),sQuery(id+"F0.wireOp",EDGE,"E11.23.9"),sQuery(id+"F0.wireOp",EDGE,"E11.23.10"),sQuery(id+"F0.wireOp",EDGE,"E11.23.11"),sQuery(id+"F0.wireOp",EDGE,"E11.23.12"),sQuery(id+"F0.wireOp",EDGE,"E11.23.13"),sQuery(id+"F0.wireOp",EDGE,"E11.24.2"),sQuery(id+"F0.wireOp",EDGE,"E11.24.3"),sQuery(id+"F0.wireOp",EDGE,"E11.24.4"),sQuery(id+"F0.wireOp",EDGE,"E11.24.5"),sQuery(id+"F0.wireOp",EDGE,"E11.24.8"),sQuery(id+"F0.wireOp",EDGE,"E11.24.9"),sQuery(id+"F0.wireOp",EDGE,"E11.24.10"),sQuery(id+"F0.wireOp",EDGE,"E11.24.11"),sQuery(id+"F0.wireOp",EDGE,"E11.24.12"),sQuery(id+"F0.wireOp",EDGE,"E11.24.13"),sQuery(id+"F0.wireOp",EDGE,"E11.25.2"),sQuery(id+"F0.wireOp",EDGE,"E11.25.3"),sQuery(id+"F0.wireOp",EDGE,"E11.25.4"),sQuery(id+"F0.wireOp",EDGE,"E11.25.5"),sQuery(id+"F0.wireOp",EDGE,"E11.25.8"),sQuery(id+"F0.wireOp",EDGE,"E11.25.9"),sQuery(id+"F0.wireOp",EDGE,"E11.25.10"),sQuery(id+"F0.wireOp",EDGE,"E11.25.11"),sQuery(id+"F0.wireOp",EDGE,"E11.25.12"),sQuery(id+"F0.wireOp",EDGE,"E11.25.13"),sQuery(id+"F0.wireOp",EDGE,"E11.26.2"),sQuery(id+"F0.wireOp",EDGE,"E11.26.3"),sQuery(id+"F0.wireOp",EDGE,"E11.26.4"),sQuery(id+"F0.wireOp",EDGE,"E11.26.5"),sQuery(id+"F0.wireOp",EDGE,"E11.26.8"),sQuery(id+"F0.wireOp",EDGE,"E11.26.9"),sQuery(id+"F0.wireOp",EDGE,"E11.26.10"),sQuery(id+"F0.wireOp",EDGE,"E11.26.11"),sQuery(id+"F0.wireOp",EDGE,"E11.26.12"),sQuery(id+"F0.wireOp",EDGE,"E11.26.13"),sQuery(id+"F0.wireOp",EDGE,"E11.27.2"),sQuery(id+"F0.wireOp",EDGE,"E11.27.3"),sQuery(id+"F0.wireOp",EDGE,"E11.27.4"),sQuery(id+"F0.wireOp",EDGE,"E11.27.5"),sQuery(id+"F0.wireOp",EDGE,"E11.27.8"),sQuery(id+"F0.wireOp",EDGE,"E11.27.9"),sQuery(id+"F0.wireOp",EDGE,"E11.27.10"),sQuery(id+"F0.wireOp",EDGE,"E11.27.11"),sQuery(id+"F0.wireOp",EDGE,"E11.27.12"),sQuery(id+"F0.wireOp",EDGE,"E11.27.13"),sQuery(id+"F0.wireOp",EDGE,"E11.28.2"),sQuery(id+"F0.wireOp",EDGE,"E11.28.3"),sQuery(id+"F0.wireOp",EDGE,"E11.28.4"),sQuery(id+"F0.wireOp",EDGE,"E11.28.5"),sQuery(id+"F0.wireOp",EDGE,"E11.28.8"),sQuery(id+"F0.wireOp",EDGE,"E11.28.9"),sQuery(id+"F0.wireOp",EDGE,"E11.28.10"),sQuery(id+"F0.wireOp",EDGE,"E11.28.11"),sQuery(id+"F0.wireOp",EDGE,"E11.28.12"),sQuery(id+"F0.wireOp",EDGE,"E11.28.13"),sQuery(id+"F0.wireOp",EDGE,"E11.29.2"),sQuery(id+"F0.wireOp",EDGE,"E11.29.3"),sQuery(id+"F0.wireOp",EDGE,"E11.29.4"),sQuery(id+"F0.wireOp",EDGE,"E11.29.5"),sQuery(id+"F0.wireOp",EDGE,"E11.29.8"),sQuery(id+"F0.wireOp",EDGE,"E11.29.9"),sQuery(id+"F0.wireOp",EDGE,"E11.29.10"),sQuery(id+"F0.wireOp",EDGE,"E11.29.11"),sQuery(id+"F0.wireOp",EDGE,"E11.29.12"),sQuery(id+"F0.wireOp",EDGE,"E11.29.13"),sQuery(id+"F0.wireOp",EDGE,"E11.30.2"),sQuery(id+"F0.wireOp",EDGE,"E11.30.3"),sQuery(id+"F0.wireOp",EDGE,"E11.30.4"),sQuery(id+"F0.wireOp",EDGE,"E11.30.5"),sQuery(id+"F0.wireOp",EDGE,"E11.30.8"),sQuery(id+"F0.wireOp",EDGE,"E11.30.9"),sQuery(id+"F0.wireOp",EDGE,"E11.30.10"),sQuery(id+"F0.wireOp",EDGE,"E11.30.11"),sQuery(id+"F0.wireOp",EDGE,"E11.30.12"),sQuery(id+"F0.wireOp",EDGE,"E11.30.13"),sQuery(id+"F0.wireOp",EDGE,"E11.31.2"),sQuery(id+"F0.wireOp",EDGE,"E11.31.3"),sQuery(id+"F0.wireOp",EDGE,"E11.31.4"),sQuery(id+"F0.wireOp",EDGE,"E11.31.5"),sQuery(id+"F0.wireOp",EDGE,"E11.31.8"),sQuery(id+"F0.wireOp",EDGE,"E11.31.9"),sQuery(id+"F0.wireOp",EDGE,"E11.31.10"),sQuery(id+"F0.wireOp",EDGE,"E11.31.11"),sQuery(id+"F0.wireOp",EDGE,"E11.31.12"),sQuery(id+"F0.wireOp",EDGE,"E11.31.13"),sQuery(id+"F0.wireOp",EDGE,"E11.32.2"),sQuery(id+"F0.wireOp",EDGE,"E11.32.3"),sQuery(id+"F0.wireOp",EDGE,"E11.32.4"),sQuery(id+"F0.wireOp",EDGE,"E11.32.5"),sQuery(id+"F0.wireOp",EDGE,"E11.32.8"),sQuery(id+"F0.wireOp",EDGE,"E11.32.9"),sQuery(id+"F0.wireOp",EDGE,"E11.32.10"),sQuery(id+"F0.wireOp",EDGE,"E11.32.11"),sQuery(id+"F0.wireOp",EDGE,"E11.32.12"),sQuery(id+"F0.wireOp",EDGE,"E11.32.13"),sQuery(id+"F0.wireOp",EDGE,"E11.33.2"),sQuery(id+"F0.wireOp",EDGE,"E11.33.3"),sQuery(id+"F0.wireOp",EDGE,"E11.33.4"),sQuery(id+"F0.wireOp",EDGE,"E11.33.5"),sQuery(id+"F0.wireOp",EDGE,"E11.33.8"),sQuery(id+"F0.wireOp",EDGE,"E11.33.9"),sQuery(id+"F0.wireOp",EDGE,"E11.33.10"),sQuery(id+"F0.wireOp",EDGE,"E11.33.11"),sQuery(id+"F0.wireOp",EDGE,"E11.33.12"),sQuery(id+"F0.wireOp",EDGE,"E11.33.13"),sQuery(id+"F0.wireOp",EDGE,"E11.34.2"),sQuery(id+"F0.wireOp",EDGE,"E11.34.3"),sQuery(id+"F0.wireOp",EDGE,"E11.34.4"),sQuery(id+"F0.wireOp",EDGE,"E11.34.5"),sQuery(id+"F0.wireOp",EDGE,"E11.34.8"),sQuery(id+"F0.wireOp",EDGE,"E11.34.9"),sQuery(id+"F0.wireOp",EDGE,"E11.34.10"),sQuery(id+"F0.wireOp",EDGE,"E11.34.11"),sQuery(id+"F0.wireOp",EDGE,"E11.34.12"),sQuery(id+"F0.wireOp",EDGE,"E11.34.13"),sQuery(id+"F0.wireOp",EDGE,"E11.35.2"),sQuery(id+"F0.wireOp",EDGE,"E11.35.3"),sQuery(id+"F0.wireOp",EDGE,"E11.35.4"),sQuery(id+"F0.wireOp",EDGE,"E11.35.5"),sQuery(id+"F0.wireOp",EDGE,"E11.35.8"),sQuery(id+"F0.wireOp",EDGE,"E11.35.9"),sQuery(id+"F0.wireOp",EDGE,"E11.35.10"),sQuery(id+"F0.wireOp",EDGE,"E11.35.11"),sQuery(id+"F0.wireOp",EDGE,"E11.35.12"),sQuery(id+"F0.wireOp",EDGE,"E11.35.13")])],"isStart":false});
            var sketch = newSketch(context, id + "F2", { "sketchPlane" : qUnion([Q0])});
            skCircle(sketch, "E12", {"center": v(0, 0) * mm, "radius": 11.43 * mm});
            skSolve(sketch);
        }
        {
            var Q0;
            Q0=makeQuery(id+"F2.imprint","IMPRINT",FACE,{"disambiguationData":[TD([[makeQuery(id+"F2.imprint","IMPRINT",EDGE,{"derivedFrom":sQuery(id+"F2.wireOp",EDGE,"E12")}),1.0]])]});
            extrude(context, id + "F3", {"entities" : qUnion([Q0]), "operationType" : NewBodyOperationType.ADD, "depth" : 7.37 * mm});
        }
        {
            var Q0;
            Q0=makeQuery(id+"F1.opExtrude","CAP_FACE",FACE,{"disambiguationData":[OSD([sQuery(id+"F0.wireOp",EDGE,"E0"),sQuery(id+"F0.wireOp",EDGE,"E1"),sQuery(id+"F0.wireOp",EDGE,"E2.trimOffspring"),sQuery(id+"F0.wireOp",EDGE,"E3"),sQuery(id+"F0.wireOp",EDGE,"E4.MirrorCS"),sQuery(id+"F0.wireOp",EDGE,"E5.MirrorCS"),sQuery(id+"F0.wireOp",EDGE,"E6.MirrorCS"),sQuery(id+"F0.wireOp",EDGE,"E7.filletArc"),sQuery(id+"F0.wireOp",EDGE,"E8.filletArc"),sQuery(id+"F0.wireOp",EDGE,"E9.filletArc"),sQuery(id+"F0.wireOp",EDGE,"E10.filletArc"),sQuery(id+"F0.wireOp",EDGE,"E11.1.2"),sQuery(id+"F0.wireOp",EDGE,"E11.1.3"),sQuery(id+"F0.wireOp",EDGE,"E11.1.4"),sQuery(id+"F0.wireOp",EDGE,"E11.1.5"),sQuery(id+"F0.wireOp",EDGE,"E11.1.8"),sQuery(id+"F0.wireOp",EDGE,"E11.1.9"),sQuery(id+"F0.wireOp",EDGE,"E11.1.10"),sQuery(id+"F0.wireOp",EDGE,"E11.1.11"),sQuery(id+"F0.wireOp",EDGE,"E11.1.12"),sQuery(id+"F0.wireOp",EDGE,"E11.1.13"),sQuery(id+"F0.wireOp",EDGE,"E11.2.2"),sQuery(id+"F0.wireOp",EDGE,"E11.2.3"),sQuery(id+"F0.wireOp",EDGE,"E11.2.4"),sQuery(id+"F0.wireOp",EDGE,"E11.2.5"),sQuery(id+"F0.wireOp",EDGE,"E11.2.8"),sQuery(id+"F0.wireOp",EDGE,"E11.2.9"),sQuery(id+"F0.wireOp",EDGE,"E11.2.10"),sQuery(id+"F0.wireOp",EDGE,"E11.2.11"),sQuery(id+"F0.wireOp",EDGE,"E11.2.12"),sQuery(id+"F0.wireOp",EDGE,"E11.2.13"),sQuery(id+"F0.wireOp",EDGE,"E11.3.2"),sQuery(id+"F0.wireOp",EDGE,"E11.3.3"),sQuery(id+"F0.wireOp",EDGE,"E11.3.4"),sQuery(id+"F0.wireOp",EDGE,"E11.3.5"),sQuery(id+"F0.wireOp",EDGE,"E11.3.8"),sQuery(id+"F0.wireOp",EDGE,"E11.3.9"),sQuery(id+"F0.wireOp",EDGE,"E11.3.10"),sQuery(id+"F0.wireOp",EDGE,"E11.3.11"),sQuery(id+"F0.wireOp",EDGE,"E11.3.12"),sQuery(id+"F0.wireOp",EDGE,"E11.3.13"),sQuery(id+"F0.wireOp",EDGE,"E11.4.2"),sQuery(id+"F0.wireOp",EDGE,"E11.4.3"),sQuery(id+"F0.wireOp",EDGE,"E11.4.4"),sQuery(id+"F0.wireOp",EDGE,"E11.4.5"),sQuery(id+"F0.wireOp",EDGE,"E11.4.8"),sQuery(id+"F0.wireOp",EDGE,"E11.4.9"),sQuery(id+"F0.wireOp",EDGE,"E11.4.10"),sQuery(id+"F0.wireOp",EDGE,"E11.4.11"),sQuery(id+"F0.wireOp",EDGE,"E11.4.12"),sQuery(id+"F0.wireOp",EDGE,"E11.4.13"),sQuery(id+"F0.wireOp",EDGE,"E11.5.2"),sQuery(id+"F0.wireOp",EDGE,"E11.5.3"),sQuery(id+"F0.wireOp",EDGE,"E11.5.4"),sQuery(id+"F0.wireOp",EDGE,"E11.5.5"),sQuery(id+"F0.wireOp",EDGE,"E11.5.8"),sQuery(id+"F0.wireOp",EDGE,"E11.5.9"),sQuery(id+"F0.wireOp",EDGE,"E11.5.10"),sQuery(id+"F0.wireOp",EDGE,"E11.5.11"),sQuery(id+"F0.wireOp",EDGE,"E11.5.12"),sQuery(id+"F0.wireOp",EDGE,"E11.5.13"),sQuery(id+"F0.wireOp",EDGE,"E11.6.2"),sQuery(id+"F0.wireOp",EDGE,"E11.6.3"),sQuery(id+"F0.wireOp",EDGE,"E11.6.4"),sQuery(id+"F0.wireOp",EDGE,"E11.6.5"),sQuery(id+"F0.wireOp",EDGE,"E11.6.8"),sQuery(id+"F0.wireOp",EDGE,"E11.6.9"),sQuery(id+"F0.wireOp",EDGE,"E11.6.10"),sQuery(id+"F0.wireOp",EDGE,"E11.6.11"),sQuery(id+"F0.wireOp",EDGE,"E11.6.12"),sQuery(id+"F0.wireOp",EDGE,"E11.6.13"),sQuery(id+"F0.wireOp",EDGE,"E11.7.2"),sQuery(id+"F0.wireOp",EDGE,"E11.7.3"),sQuery(id+"F0.wireOp",EDGE,"E11.7.4"),sQuery(id+"F0.wireOp",EDGE,"E11.7.5"),sQuery(id+"F0.wireOp",EDGE,"E11.7.8"),sQuery(id+"F0.wireOp",EDGE,"E11.7.9"),sQuery(id+"F0.wireOp",EDGE,"E11.7.10"),sQuery(id+"F0.wireOp",EDGE,"E11.7.11"),sQuery(id+"F0.wireOp",EDGE,"E11.7.12"),sQuery(id+"F0.wireOp",EDGE,"E11.7.13"),sQuery(id+"F0.wireOp",EDGE,"E11.8.2"),sQuery(id+"F0.wireOp",EDGE,"E11.8.3"),sQuery(id+"F0.wireOp",EDGE,"E11.8.4"),sQuery(id+"F0.wireOp",EDGE,"E11.8.5"),sQuery(id+"F0.wireOp",EDGE,"E11.8.8"),sQuery(id+"F0.wireOp",EDGE,"E11.8.9"),sQuery(id+"F0.wireOp",EDGE,"E11.8.10"),sQuery(id+"F0.wireOp",EDGE,"E11.8.11"),sQuery(id+"F0.wireOp",EDGE,"E11.8.12"),sQuery(id+"F0.wireOp",EDGE,"E11.8.13"),sQuery(id+"F0.wireOp",EDGE,"E11.9.2"),sQuery(id+"F0.wireOp",EDGE,"E11.9.3"),sQuery(id+"F0.wireOp",EDGE,"E11.9.4"),sQuery(id+"F0.wireOp",EDGE,"E11.9.5"),sQuery(id+"F0.wireOp",EDGE,"E11.9.8"),sQuery(id+"F0.wireOp",EDGE,"E11.9.9"),sQuery(id+"F0.wireOp",EDGE,"E11.9.10"),sQuery(id+"F0.wireOp",EDGE,"E11.9.11"),sQuery(id+"F0.wireOp",EDGE,"E11.9.12"),sQuery(id+"F0.wireOp",EDGE,"E11.9.13"),sQuery(id+"F0.wireOp",EDGE,"E11.10.2"),sQuery(id+"F0.wireOp",EDGE,"E11.10.3"),sQuery(id+"F0.wireOp",EDGE,"E11.10.4"),sQuery(id+"F0.wireOp",EDGE,"E11.10.5"),sQuery(id+"F0.wireOp",EDGE,"E11.10.8"),sQuery(id+"F0.wireOp",EDGE,"E11.10.9"),sQuery(id+"F0.wireOp",EDGE,"E11.10.10"),sQuery(id+"F0.wireOp",EDGE,"E11.10.11"),sQuery(id+"F0.wireOp",EDGE,"E11.10.12"),sQuery(id+"F0.wireOp",EDGE,"E11.10.13"),sQuery(id+"F0.wireOp",EDGE,"E11.11.2"),sQuery(id+"F0.wireOp",EDGE,"E11.11.3"),sQuery(id+"F0.wireOp",EDGE,"E11.11.4"),sQuery(id+"F0.wireOp",EDGE,"E11.11.5"),sQuery(id+"F0.wireOp",EDGE,"E11.11.8"),sQuery(id+"F0.wireOp",EDGE,"E11.11.9"),sQuery(id+"F0.wireOp",EDGE,"E11.11.10"),sQuery(id+"F0.wireOp",EDGE,"E11.11.11"),sQuery(id+"F0.wireOp",EDGE,"E11.11.12"),sQuery(id+"F0.wireOp",EDGE,"E11.11.13"),sQuery(id+"F0.wireOp",EDGE,"E11.12.2"),sQuery(id+"F0.wireOp",EDGE,"E11.12.3"),sQuery(id+"F0.wireOp",EDGE,"E11.12.4"),sQuery(id+"F0.wireOp",EDGE,"E11.12.5"),sQuery(id+"F0.wireOp",EDGE,"E11.12.8"),sQuery(id+"F0.wireOp",EDGE,"E11.12.9"),sQuery(id+"F0.wireOp",EDGE,"E11.12.10"),sQuery(id+"F0.wireOp",EDGE,"E11.12.11"),sQuery(id+"F0.wireOp",EDGE,"E11.12.12"),sQuery(id+"F0.wireOp",EDGE,"E11.12.13"),sQuery(id+"F0.wireOp",EDGE,"E11.13.2"),sQuery(id+"F0.wireOp",EDGE,"E11.13.3"),sQuery(id+"F0.wireOp",EDGE,"E11.13.4"),sQuery(id+"F0.wireOp",EDGE,"E11.13.5"),sQuery(id+"F0.wireOp",EDGE,"E11.13.8"),sQuery(id+"F0.wireOp",EDGE,"E11.13.9"),sQuery(id+"F0.wireOp",EDGE,"E11.13.10"),sQuery(id+"F0.wireOp",EDGE,"E11.13.11"),sQuery(id+"F0.wireOp",EDGE,"E11.13.12"),sQuery(id+"F0.wireOp",EDGE,"E11.13.13"),sQuery(id+"F0.wireOp",EDGE,"E11.14.2"),sQuery(id+"F0.wireOp",EDGE,"E11.14.3"),sQuery(id+"F0.wireOp",EDGE,"E11.14.4"),sQuery(id+"F0.wireOp",EDGE,"E11.14.5"),sQuery(id+"F0.wireOp",EDGE,"E11.14.8"),sQuery(id+"F0.wireOp",EDGE,"E11.14.9"),sQuery(id+"F0.wireOp",EDGE,"E11.14.10"),sQuery(id+"F0.wireOp",EDGE,"E11.14.11"),sQuery(id+"F0.wireOp",EDGE,"E11.14.12"),sQuery(id+"F0.wireOp",EDGE,"E11.14.13"),sQuery(id+"F0.wireOp",EDGE,"E11.15.2"),sQuery(id+"F0.wireOp",EDGE,"E11.15.3"),sQuery(id+"F0.wireOp",EDGE,"E11.15.4"),sQuery(id+"F0.wireOp",EDGE,"E11.15.5"),sQuery(id+"F0.wireOp",EDGE,"E11.15.8"),sQuery(id+"F0.wireOp",EDGE,"E11.15.9"),sQuery(id+"F0.wireOp",EDGE,"E11.15.10"),sQuery(id+"F0.wireOp",EDGE,"E11.15.11"),sQuery(id+"F0.wireOp",EDGE,"E11.15.12"),sQuery(id+"F0.wireOp",EDGE,"E11.15.13"),sQuery(id+"F0.wireOp",EDGE,"E11.16.2"),sQuery(id+"F0.wireOp",EDGE,"E11.16.3"),sQuery(id+"F0.wireOp",EDGE,"E11.16.4"),sQuery(id+"F0.wireOp",EDGE,"E11.16.5"),sQuery(id+"F0.wireOp",EDGE,"E11.16.8"),sQuery(id+"F0.wireOp",EDGE,"E11.16.9"),sQuery(id+"F0.wireOp",EDGE,"E11.16.10"),sQuery(id+"F0.wireOp",EDGE,"E11.16.11"),sQuery(id+"F0.wireOp",EDGE,"E11.16.12"),sQuery(id+"F0.wireOp",EDGE,"E11.16.13"),sQuery(id+"F0.wireOp",EDGE,"E11.17.2"),sQuery(id+"F0.wireOp",EDGE,"E11.17.3"),sQuery(id+"F0.wireOp",EDGE,"E11.17.4"),sQuery(id+"F0.wireOp",EDGE,"E11.17.5"),sQuery(id+"F0.wireOp",EDGE,"E11.17.8"),sQuery(id+"F0.wireOp",EDGE,"E11.17.9"),sQuery(id+"F0.wireOp",EDGE,"E11.17.10"),sQuery(id+"F0.wireOp",EDGE,"E11.17.11"),sQuery(id+"F0.wireOp",EDGE,"E11.17.12"),sQuery(id+"F0.wireOp",EDGE,"E11.17.13"),sQuery(id+"F0.wireOp",EDGE,"E11.18.2"),sQuery(id+"F0.wireOp",EDGE,"E11.18.3"),sQuery(id+"F0.wireOp",EDGE,"E11.18.4"),sQuery(id+"F0.wireOp",EDGE,"E11.18.5"),sQuery(id+"F0.wireOp",EDGE,"E11.18.8"),sQuery(id+"F0.wireOp",EDGE,"E11.18.9"),sQuery(id+"F0.wireOp",EDGE,"E11.18.10"),sQuery(id+"F0.wireOp",EDGE,"E11.18.11"),sQuery(id+"F0.wireOp",EDGE,"E11.18.12"),sQuery(id+"F0.wireOp",EDGE,"E11.18.13"),sQuery(id+"F0.wireOp",EDGE,"E11.19.2"),sQuery(id+"F0.wireOp",EDGE,"E11.19.3"),sQuery(id+"F0.wireOp",EDGE,"E11.19.4"),sQuery(id+"F0.wireOp",EDGE,"E11.19.5"),sQuery(id+"F0.wireOp",EDGE,"E11.19.8"),sQuery(id+"F0.wireOp",EDGE,"E11.19.9"),sQuery(id+"F0.wireOp",EDGE,"E11.19.10"),sQuery(id+"F0.wireOp",EDGE,"E11.19.11"),sQuery(id+"F0.wireOp",EDGE,"E11.19.12"),sQuery(id+"F0.wireOp",EDGE,"E11.19.13"),sQuery(id+"F0.wireOp",EDGE,"E11.20.2"),sQuery(id+"F0.wireOp",EDGE,"E11.20.3"),sQuery(id+"F0.wireOp",EDGE,"E11.20.4"),sQuery(id+"F0.wireOp",EDGE,"E11.20.5"),sQuery(id+"F0.wireOp",EDGE,"E11.20.8"),sQuery(id+"F0.wireOp",EDGE,"E11.20.9"),sQuery(id+"F0.wireOp",EDGE,"E11.20.10"),sQuery(id+"F0.wireOp",EDGE,"E11.20.11"),sQuery(id+"F0.wireOp",EDGE,"E11.20.12"),sQuery(id+"F0.wireOp",EDGE,"E11.20.13"),sQuery(id+"F0.wireOp",EDGE,"E11.21.2"),sQuery(id+"F0.wireOp",EDGE,"E11.21.3"),sQuery(id+"F0.wireOp",EDGE,"E11.21.4"),sQuery(id+"F0.wireOp",EDGE,"E11.21.5"),sQuery(id+"F0.wireOp",EDGE,"E11.21.8"),sQuery(id+"F0.wireOp",EDGE,"E11.21.9"),sQuery(id+"F0.wireOp",EDGE,"E11.21.10"),sQuery(id+"F0.wireOp",EDGE,"E11.21.11"),sQuery(id+"F0.wireOp",EDGE,"E11.21.12"),sQuery(id+"F0.wireOp",EDGE,"E11.21.13"),sQuery(id+"F0.wireOp",EDGE,"E11.22.2"),sQuery(id+"F0.wireOp",EDGE,"E11.22.3"),sQuery(id+"F0.wireOp",EDGE,"E11.22.4"),sQuery(id+"F0.wireOp",EDGE,"E11.22.5"),sQuery(id+"F0.wireOp",EDGE,"E11.22.8"),sQuery(id+"F0.wireOp",EDGE,"E11.22.9"),sQuery(id+"F0.wireOp",EDGE,"E11.22.10"),sQuery(id+"F0.wireOp",EDGE,"E11.22.11"),sQuery(id+"F0.wireOp",EDGE,"E11.22.12"),sQuery(id+"F0.wireOp",EDGE,"E11.22.13"),sQuery(id+"F0.wireOp",EDGE,"E11.23.2"),sQuery(id+"F0.wireOp",EDGE,"E11.23.3"),sQuery(id+"F0.wireOp",EDGE,"E11.23.4"),sQuery(id+"F0.wireOp",EDGE,"E11.23.5"),sQuery(id+"F0.wireOp",EDGE,"E11.23.8"),sQuery(id+"F0.wireOp",EDGE,"E11.23.9"),sQuery(id+"F0.wireOp",EDGE,"E11.23.10"),sQuery(id+"F0.wireOp",EDGE,"E11.23.11"),sQuery(id+"F0.wireOp",EDGE,"E11.23.12"),sQuery(id+"F0.wireOp",EDGE,"E11.23.13"),sQuery(id+"F0.wireOp",EDGE,"E11.24.2"),sQuery(id+"F0.wireOp",EDGE,"E11.24.3"),sQuery(id+"F0.wireOp",EDGE,"E11.24.4"),sQuery(id+"F0.wireOp",EDGE,"E11.24.5"),sQuery(id+"F0.wireOp",EDGE,"E11.24.8"),sQuery(id+"F0.wireOp",EDGE,"E11.24.9"),sQuery(id+"F0.wireOp",EDGE,"E11.24.10"),sQuery(id+"F0.wireOp",EDGE,"E11.24.11"),sQuery(id+"F0.wireOp",EDGE,"E11.24.12"),sQuery(id+"F0.wireOp",EDGE,"E11.24.13"),sQuery(id+"F0.wireOp",EDGE,"E11.25.2"),sQuery(id+"F0.wireOp",EDGE,"E11.25.3"),sQuery(id+"F0.wireOp",EDGE,"E11.25.4"),sQuery(id+"F0.wireOp",EDGE,"E11.25.5"),sQuery(id+"F0.wireOp",EDGE,"E11.25.8"),sQuery(id+"F0.wireOp",EDGE,"E11.25.9"),sQuery(id+"F0.wireOp",EDGE,"E11.25.10"),sQuery(id+"F0.wireOp",EDGE,"E11.25.11"),sQuery(id+"F0.wireOp",EDGE,"E11.25.12"),sQuery(id+"F0.wireOp",EDGE,"E11.25.13"),sQuery(id+"F0.wireOp",EDGE,"E11.26.2"),sQuery(id+"F0.wireOp",EDGE,"E11.26.3"),sQuery(id+"F0.wireOp",EDGE,"E11.26.4"),sQuery(id+"F0.wireOp",EDGE,"E11.26.5"),sQuery(id+"F0.wireOp",EDGE,"E11.26.8"),sQuery(id+"F0.wireOp",EDGE,"E11.26.9"),sQuery(id+"F0.wireOp",EDGE,"E11.26.10"),sQuery(id+"F0.wireOp",EDGE,"E11.26.11"),sQuery(id+"F0.wireOp",EDGE,"E11.26.12"),sQuery(id+"F0.wireOp",EDGE,"E11.26.13"),sQuery(id+"F0.wireOp",EDGE,"E11.27.2"),sQuery(id+"F0.wireOp",EDGE,"E11.27.3"),sQuery(id+"F0.wireOp",EDGE,"E11.27.4"),sQuery(id+"F0.wireOp",EDGE,"E11.27.5"),sQuery(id+"F0.wireOp",EDGE,"E11.27.8"),sQuery(id+"F0.wireOp",EDGE,"E11.27.9"),sQuery(id+"F0.wireOp",EDGE,"E11.27.10"),sQuery(id+"F0.wireOp",EDGE,"E11.27.11"),sQuery(id+"F0.wireOp",EDGE,"E11.27.12"),sQuery(id+"F0.wireOp",EDGE,"E11.27.13"),sQuery(id+"F0.wireOp",EDGE,"E11.28.2"),sQuery(id+"F0.wireOp",EDGE,"E11.28.3"),sQuery(id+"F0.wireOp",EDGE,"E11.28.4"),sQuery(id+"F0.wireOp",EDGE,"E11.28.5"),sQuery(id+"F0.wireOp",EDGE,"E11.28.8"),sQuery(id+"F0.wireOp",EDGE,"E11.28.9"),sQuery(id+"F0.wireOp",EDGE,"E11.28.10"),sQuery(id+"F0.wireOp",EDGE,"E11.28.11"),sQuery(id+"F0.wireOp",EDGE,"E11.28.12"),sQuery(id+"F0.wireOp",EDGE,"E11.28.13"),sQuery(id+"F0.wireOp",EDGE,"E11.29.2"),sQuery(id+"F0.wireOp",EDGE,"E11.29.3"),sQuery(id+"F0.wireOp",EDGE,"E11.29.4"),sQuery(id+"F0.wireOp",EDGE,"E11.29.5"),sQuery(id+"F0.wireOp",EDGE,"E11.29.8"),sQuery(id+"F0.wireOp",EDGE,"E11.29.9"),sQuery(id+"F0.wireOp",EDGE,"E11.29.10"),sQuery(id+"F0.wireOp",EDGE,"E11.29.11"),sQuery(id+"F0.wireOp",EDGE,"E11.29.12"),sQuery(id+"F0.wireOp",EDGE,"E11.29.13"),sQuery(id+"F0.wireOp",EDGE,"E11.30.2"),sQuery(id+"F0.wireOp",EDGE,"E11.30.3"),sQuery(id+"F0.wireOp",EDGE,"E11.30.4"),sQuery(id+"F0.wireOp",EDGE,"E11.30.5"),sQuery(id+"F0.wireOp",EDGE,"E11.30.8"),sQuery(id+"F0.wireOp",EDGE,"E11.30.9"),sQuery(id+"F0.wireOp",EDGE,"E11.30.10"),sQuery(id+"F0.wireOp",EDGE,"E11.30.11"),sQuery(id+"F0.wireOp",EDGE,"E11.30.12"),sQuery(id+"F0.wireOp",EDGE,"E11.30.13"),sQuery(id+"F0.wireOp",EDGE,"E11.31.2"),sQuery(id+"F0.wireOp",EDGE,"E11.31.3"),sQuery(id+"F0.wireOp",EDGE,"E11.31.4"),sQuery(id+"F0.wireOp",EDGE,"E11.31.5"),sQuery(id+"F0.wireOp",EDGE,"E11.31.8"),sQuery(id+"F0.wireOp",EDGE,"E11.31.9"),sQuery(id+"F0.wireOp",EDGE,"E11.31.10"),sQuery(id+"F0.wireOp",EDGE,"E11.31.11"),sQuery(id+"F0.wireOp",EDGE,"E11.31.12"),sQuery(id+"F0.wireOp",EDGE,"E11.31.13"),sQuery(id+"F0.wireOp",EDGE,"E11.32.2"),sQuery(id+"F0.wireOp",EDGE,"E11.32.3"),sQuery(id+"F0.wireOp",EDGE,"E11.32.4"),sQuery(id+"F0.wireOp",EDGE,"E11.32.5"),sQuery(id+"F0.wireOp",EDGE,"E11.32.8"),sQuery(id+"F0.wireOp",EDGE,"E11.32.9"),sQuery(id+"F0.wireOp",EDGE,"E11.32.10"),sQuery(id+"F0.wireOp",EDGE,"E11.32.11"),sQuery(id+"F0.wireOp",EDGE,"E11.32.12"),sQuery(id+"F0.wireOp",EDGE,"E11.32.13"),sQuery(id+"F0.wireOp",EDGE,"E11.33.2"),sQuery(id+"F0.wireOp",EDGE,"E11.33.3"),sQuery(id+"F0.wireOp",EDGE,"E11.33.4"),sQuery(id+"F0.wireOp",EDGE,"E11.33.5"),sQuery(id+"F0.wireOp",EDGE,"E11.33.8"),sQuery(id+"F0.wireOp",EDGE,"E11.33.9"),sQuery(id+"F0.wireOp",EDGE,"E11.33.10"),sQuery(id+"F0.wireOp",EDGE,"E11.33.11"),sQuery(id+"F0.wireOp",EDGE,"E11.33.12"),sQuery(id+"F0.wireOp",EDGE,"E11.33.13"),sQuery(id+"F0.wireOp",EDGE,"E11.34.2"),sQuery(id+"F0.wireOp",EDGE,"E11.34.3"),sQuery(id+"F0.wireOp",EDGE,"E11.34.4"),sQuery(id+"F0.wireOp",EDGE,"E11.34.5"),sQuery(id+"F0.wireOp",EDGE,"E11.34.8"),sQuery(id+"F0.wireOp",EDGE,"E11.34.9"),sQuery(id+"F0.wireOp",EDGE,"E11.34.10"),sQuery(id+"F0.wireOp",EDGE,"E11.34.11"),sQuery(id+"F0.wireOp",EDGE,"E11.34.12"),sQuery(id+"F0.wireOp",EDGE,"E11.34.13"),sQuery(id+"F0.wireOp",EDGE,"E11.35.2"),sQuery(id+"F0.wireOp",EDGE,"E11.35.3"),sQuery(id+"F0.wireOp",EDGE,"E11.35.4"),sQuery(id+"F0.wireOp",EDGE,"E11.35.5"),sQuery(id+"F0.wireOp",EDGE,"E11.35.8"),sQuery(id+"F0.wireOp",EDGE,"E11.35.9"),sQuery(id+"F0.wireOp",EDGE,"E11.35.10"),sQuery(id+"F0.wireOp",EDGE,"E11.35.11"),sQuery(id+"F0.wireOp",EDGE,"E11.35.12"),sQuery(id+"F0.wireOp",EDGE,"E11.35.13")])],"isStart":true});
            var sketch = newSketch(context, id + "F4", { "sketchPlane" : qUnion([Q0])});
            skCircle(sketch, "E13", {"center": v(0, 0) * mm, "radius": 5.59 * mm});
            skSolve(sketch);
        }
        {
            var Q0;
            Q0=makeQuery(id+"F4.imprint","IMPRINT",FACE,{"disambiguationData":[TD([[makeQuery(id+"F4.imprint","IMPRINT",EDGE,{"derivedFrom":sQuery(id+"F4.wireOp",EDGE,"E13")}),1.0]])]});
            extrude(context, id + "F5", {"entities" : qUnion([Q0]), "operationType" : NewBodyOperationType.REMOVE, "oppositeDirection" : true, "depth" : 24.83 * mm});
        }
    });
